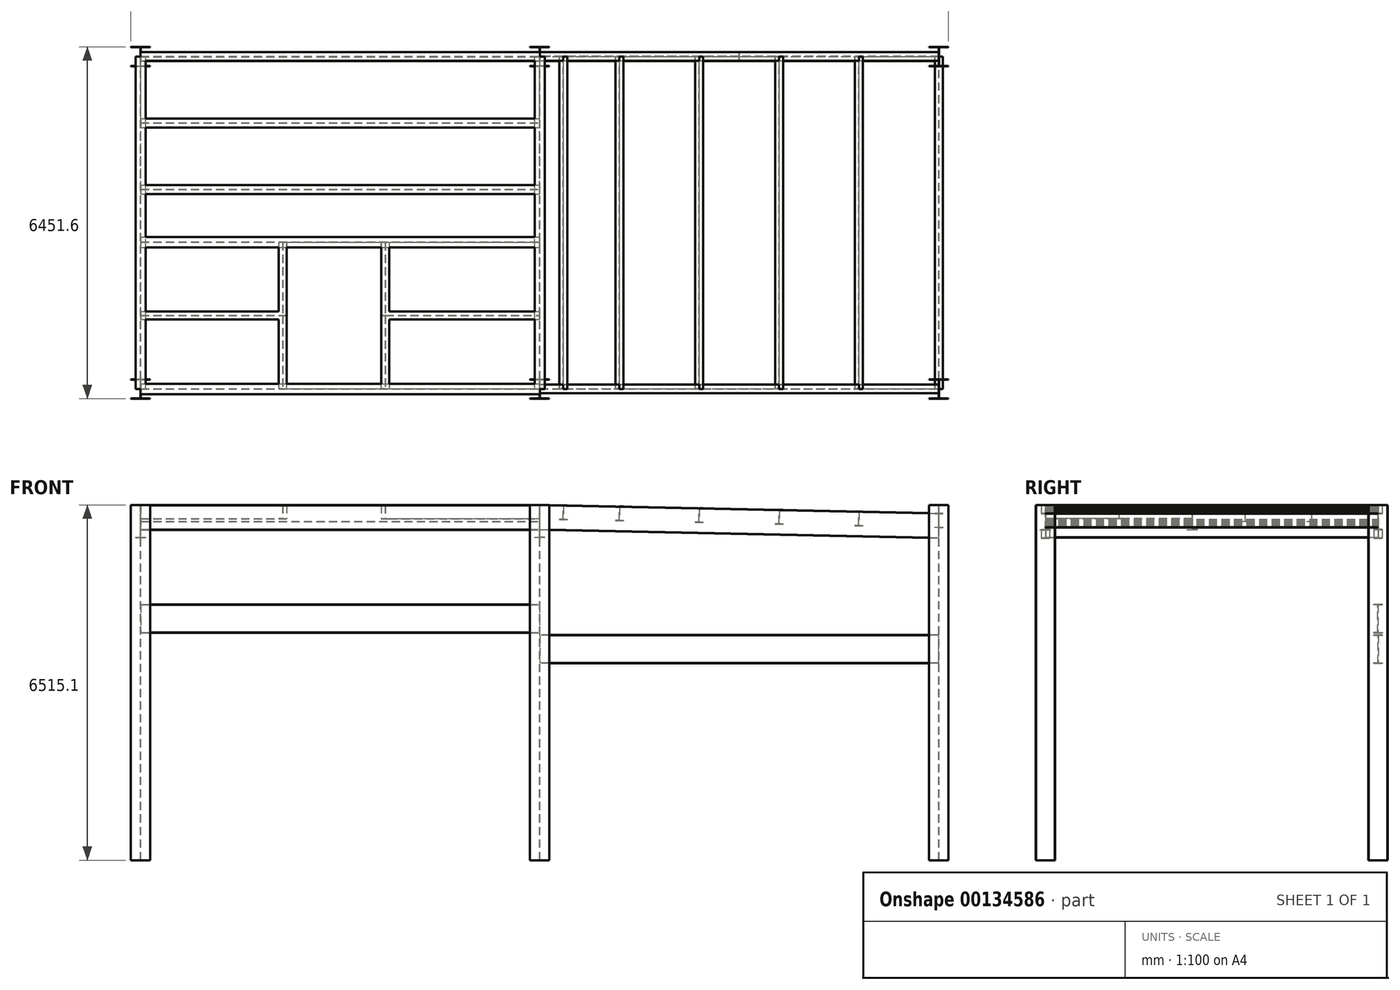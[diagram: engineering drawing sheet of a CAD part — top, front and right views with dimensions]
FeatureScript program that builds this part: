
annotation { "Feature Type Name" : "Feature", "Feature Type Description" : "" }
export const myFeature = defineFeature(function(context is Context, id is Id, definition is map)
    precondition{}
    {
        {
            var Q0;
            Q0=qCreatedBy(makeId("Top.planeOp"),FACE);
            var sketch = newSketch(context, id + "F0", { "sketchPlane" : qUnion([Q0])});
            skLineSegment(sketch, "E0", {"start": v(0, 0) * mm, "end": v(0, 177.8) * mm, "construction": true});
            skLineSegment(sketch, "E1", {"start": v(0, 0) * mm, "end": v(-3.18, 0) * mm, "construction": true});
            skLineSegment(sketch, "E2", {"start": v(0, 177.8) * mm, "end": v(-177.8, 177.8) * mm});
            skLineSegment(sketch, "E3", {"start": v(-177.8, 177.8) * mm, "end": v(-177.8, 171.45) * mm});
            skLineSegment(sketch, "E4", {"start": v(-177.8, 171.45) * mm, "end": v(-3.17, 171.45) * mm});
            skLineSegment(sketch, "E5", {"start": v(-3.17, 171.45) * mm, "end": v(-3.17, 0) * mm});
            skLineSegment(sketch, "E6.MirrorCS", {"start": v(177.8, 177.8) * mm, "end": v(177.8, 171.45) * mm});
            skLineSegment(sketch, "E7.MirrorCS", {"start": v(0, 177.8) * mm, "end": v(177.8, 177.8) * mm});
            skLineSegment(sketch, "E8.MirrorCS", {"start": v(3.17, 171.45) * mm, "end": v(3.17, 0) * mm});
            skLineSegment(sketch, "E9.MirrorCS", {"start": v(177.8, 171.45) * mm, "end": v(3.17, 171.45) * mm});
            skLineSegment(sketch, "E10.MirrorCS", {"start": v(-177.8, -171.45) * mm, "end": v(-3.18, -171.45) * mm});
            skLineSegment(sketch, "E11.MirrorCS", {"start": v(-3.17, -171.45) * mm, "end": v(-3.17, 0) * mm});
            skLineSegment(sketch, "E12.MirrorCS", {"start": v(0, -177.8) * mm, "end": v(177.8, -177.8) * mm});
            skLineSegment(sketch, "E13.MirrorCS", {"start": v(3.18, -171.45) * mm, "end": v(3.17, 0) * mm});
            skLineSegment(sketch, "E14.MirrorCS", {"start": v(177.8, -177.8) * mm, "end": v(177.8, -171.45) * mm});
            skLineSegment(sketch, "E15.MirrorCS", {"start": v(177.8, -171.45) * mm, "end": v(3.18, -171.45) * mm});
            skLineSegment(sketch, "E16.MirrorCS", {"start": v(-177.8, -177.8) * mm, "end": v(-177.8, -171.45) * mm});
            skLineSegment(sketch, "E17.MirrorCS", {"start": v(0, -177.8) * mm, "end": v(-177.8, -177.8) * mm});
            skLineSegment(sketch, "E18", {"start": v(-3.17, 171.45) * mm, "end": v(3.17, 171.45) * mm, "construction": true});
            skLineSegment(sketch, "E19.0.1.0", {"start": v(0, -6096) * mm, "end": v(0, -5918.2) * mm, "construction": true});
            skLineSegment(sketch, "E19.0.1.1", {"start": v(177.8, -5924.55) * mm, "end": v(3.17, -5924.55) * mm});
            skLineSegment(sketch, "E19.0.1.2", {"start": v(-3.17, -5924.55) * mm, "end": v(-3.17, -6096) * mm});
            skLineSegment(sketch, "E19.0.1.3", {"start": v(-177.8, -5924.55) * mm, "end": v(-3.17, -5924.55) * mm});
            skLineSegment(sketch, "E19.0.1.4", {"start": v(0, -5918.2) * mm, "end": v(177.8, -5918.2) * mm});
            skLineSegment(sketch, "E19.0.1.5", {"start": v(0, -6273.8) * mm, "end": v(-177.8, -6273.8) * mm});
            skLineSegment(sketch, "E19.0.1.6", {"start": v(3.17, -5924.55) * mm, "end": v(3.17, -6096) * mm});
            skLineSegment(sketch, "E19.0.1.7", {"start": v(-177.8, -6267.45) * mm, "end": v(-3.18, -6267.45) * mm});
            skLineSegment(sketch, "E19.0.1.8", {"start": v(3.18, -6267.45) * mm, "end": v(3.17, -6096) * mm});
            skLineSegment(sketch, "E19.0.1.9", {"start": v(-3.17, -6267.45) * mm, "end": v(-3.17, -6096) * mm});
            skLineSegment(sketch, "E19.0.1.10", {"start": v(0, -6273.8) * mm, "end": v(177.8, -6273.8) * mm});
            skLineSegment(sketch, "E19.0.1.11", {"start": v(0, -5918.2) * mm, "end": v(-177.8, -5918.2) * mm});
            skLineSegment(sketch, "E19.0.1.12", {"start": v(177.8, -6267.45) * mm, "end": v(3.18, -6267.45) * mm});
            skLineSegment(sketch, "E19.0.1.13", {"start": v(177.8, -6273.8) * mm, "end": v(177.8, -6267.45) * mm});
            skLineSegment(sketch, "E19.0.1.14", {"start": v(177.8, -5918.2) * mm, "end": v(177.8, -5924.55) * mm});
            skLineSegment(sketch, "E19.0.1.15", {"start": v(-177.8, -5918.2) * mm, "end": v(-177.8, -5924.55) * mm});
            skLineSegment(sketch, "E19.0.1.16", {"start": v(-177.8, -6273.8) * mm, "end": v(-177.8, -6267.45) * mm});
            skLineSegment(sketch, "E19.0.1.17", {"start": v(0, -6096) * mm, "end": v(-3.17, -6096) * mm, "construction": true});
            skLineSegment(sketch, "E19.0.1.18", {"start": v(-3.17, -5924.55) * mm, "end": v(3.17, -5924.55) * mm, "construction": true});
            skLineSegment(sketch, "E19.1.0.0", {"start": v(-7315.2, 0) * mm, "end": v(-7315.2, 177.8) * mm, "construction": true});
            skLineSegment(sketch, "E19.1.0.1", {"start": v(-7137.4, 171.45) * mm, "end": v(-7312.03, 171.45) * mm});
            skLineSegment(sketch, "E19.1.0.2", {"start": v(-7318.38, 171.45) * mm, "end": v(-7318.38, 0) * mm});
            skLineSegment(sketch, "E19.1.0.3", {"start": v(-7493, 171.45) * mm, "end": v(-7318.38, 171.45) * mm});
            skLineSegment(sketch, "E19.1.0.4", {"start": v(-7315.2, 177.8) * mm, "end": v(-7137.4, 177.8) * mm});
            skLineSegment(sketch, "E19.1.0.5", {"start": v(-7315.2, -177.8) * mm, "end": v(-7493, -177.8) * mm});
            skLineSegment(sketch, "E19.1.0.6", {"start": v(-7312.03, 171.45) * mm, "end": v(-7312.03, 0) * mm});
            skLineSegment(sketch, "E19.1.0.7", {"start": v(-7493, -171.45) * mm, "end": v(-7318.38, -171.45) * mm});
            skLineSegment(sketch, "E19.1.0.8", {"start": v(-7312.03, -171.45) * mm, "end": v(-7312.03, 0) * mm});
            skLineSegment(sketch, "E19.1.0.9", {"start": v(-7318.38, -171.45) * mm, "end": v(-7318.38, 0) * mm});
            skLineSegment(sketch, "E19.1.0.10", {"start": v(-7315.2, -177.8) * mm, "end": v(-7137.4, -177.8) * mm});
            skLineSegment(sketch, "E19.1.0.11", {"start": v(-7315.2, 177.8) * mm, "end": v(-7493, 177.8) * mm});
            skLineSegment(sketch, "E19.1.0.12", {"start": v(-7137.4, -171.45) * mm, "end": v(-7312.03, -171.45) * mm});
            skLineSegment(sketch, "E19.1.0.13", {"start": v(-7137.4, -177.8) * mm, "end": v(-7137.4, -171.45) * mm});
            skLineSegment(sketch, "E19.1.0.14", {"start": v(-7137.4, 177.8) * mm, "end": v(-7137.4, 171.45) * mm});
            skLineSegment(sketch, "E19.1.0.15", {"start": v(-7493, 177.8) * mm, "end": v(-7493, 171.45) * mm});
            skLineSegment(sketch, "E19.1.0.16", {"start": v(-7493, -177.8) * mm, "end": v(-7493, -171.45) * mm});
            skLineSegment(sketch, "E19.1.0.17", {"start": v(-7315.2, 0) * mm, "end": v(-7318.38, 0) * mm, "construction": true});
            skLineSegment(sketch, "E19.1.0.18", {"start": v(-7318.38, 171.45) * mm, "end": v(-7312.03, 171.45) * mm, "construction": true});
            skLineSegment(sketch, "E19.1.1.0", {"start": v(-7315.2, -6096) * mm, "end": v(-7315.2, -5918.2) * mm, "construction": true});
            skLineSegment(sketch, "E19.1.1.1", {"start": v(-7137.4, -5924.55) * mm, "end": v(-7312.03, -5924.55) * mm});
            skLineSegment(sketch, "E19.1.1.2", {"start": v(-7318.38, -5924.55) * mm, "end": v(-7318.38, -6096) * mm});
            skLineSegment(sketch, "E19.1.1.3", {"start": v(-7493, -5924.55) * mm, "end": v(-7318.38, -5924.55) * mm});
            skLineSegment(sketch, "E19.1.1.4", {"start": v(-7315.2, -5918.2) * mm, "end": v(-7137.4, -5918.2) * mm});
            skLineSegment(sketch, "E19.1.1.5", {"start": v(-7315.2, -6273.8) * mm, "end": v(-7493, -6273.8) * mm});
            skLineSegment(sketch, "E19.1.1.6", {"start": v(-7312.03, -5924.55) * mm, "end": v(-7312.03, -6096) * mm});
            skLineSegment(sketch, "E19.1.1.7", {"start": v(-7493, -6267.45) * mm, "end": v(-7318.38, -6267.45) * mm});
            skLineSegment(sketch, "E19.1.1.8", {"start": v(-7312.03, -6267.45) * mm, "end": v(-7312.03, -6096) * mm});
            skLineSegment(sketch, "E19.1.1.9", {"start": v(-7318.38, -6267.45) * mm, "end": v(-7318.38, -6096) * mm});
            skLineSegment(sketch, "E19.1.1.10", {"start": v(-7315.2, -6273.8) * mm, "end": v(-7137.4, -6273.8) * mm});
            skLineSegment(sketch, "E19.1.1.11", {"start": v(-7315.2, -5918.2) * mm, "end": v(-7493, -5918.2) * mm});
            skLineSegment(sketch, "E19.1.1.12", {"start": v(-7137.4, -6267.45) * mm, "end": v(-7312.03, -6267.45) * mm});
            skLineSegment(sketch, "E19.1.1.13", {"start": v(-7137.4, -6273.8) * mm, "end": v(-7137.4, -6267.45) * mm});
            skLineSegment(sketch, "E19.1.1.14", {"start": v(-7137.4, -5918.2) * mm, "end": v(-7137.4, -5924.55) * mm});
            skLineSegment(sketch, "E19.1.1.15", {"start": v(-7493, -5918.2) * mm, "end": v(-7493, -5924.55) * mm});
            skLineSegment(sketch, "E19.1.1.16", {"start": v(-7493, -6273.8) * mm, "end": v(-7493, -6267.45) * mm});
            skLineSegment(sketch, "E19.1.1.17", {"start": v(-7315.2, -6096) * mm, "end": v(-7318.38, -6096) * mm, "construction": true});
            skLineSegment(sketch, "E19.1.1.18", {"start": v(-7318.38, -5924.55) * mm, "end": v(-7312.03, -5924.55) * mm, "construction": true});
            skLineSegment(sketch, "E19.direction1", {"start": v(-177.8, -177.8) * mm, "end": v(-7493, -177.8) * mm, "construction": true});
            skLineSegment(sketch, "E19.direction2", {"start": v(-177.8, -177.8) * mm, "end": v(-177.8, -6273.8) * mm, "construction": true});
            skLineSegment(sketch, "E20.1.0.0", {"start": v(7315.2, -5918.2) * mm, "end": v(7493, -5918.2) * mm});
            skLineSegment(sketch, "E20.1.0.1", {"start": v(7315.2, -6273.8) * mm, "end": v(7137.4, -6273.8) * mm});
            skLineSegment(sketch, "E20.1.0.2", {"start": v(7312.03, -5924.55) * mm, "end": v(7312.03, -6096) * mm});
            skLineSegment(sketch, "E20.1.0.3", {"start": v(7137.4, -5924.55) * mm, "end": v(7312.03, -5924.55) * mm});
            skLineSegment(sketch, "E20.1.0.4", {"start": v(7315.2, -6096) * mm, "end": v(7315.2, -5918.2) * mm, "construction": true});
            skLineSegment(sketch, "E20.1.0.5", {"start": v(7315.2, -6273.8) * mm, "end": v(7493, -6273.8) * mm});
            skLineSegment(sketch, "E20.1.0.6", {"start": v(7315.2, -5918.2) * mm, "end": v(7137.4, -5918.2) * mm});
            skLineSegment(sketch, "E20.1.0.7", {"start": v(7318.38, -6267.45) * mm, "end": v(7318.38, -6096) * mm});
            skLineSegment(sketch, "E20.1.0.8", {"start": v(7312.03, -6267.45) * mm, "end": v(7312.03, -6096) * mm});
            skLineSegment(sketch, "E20.1.0.9", {"start": v(7493, -6267.45) * mm, "end": v(7318.38, -6267.45) * mm});
            skLineSegment(sketch, "E20.1.0.10", {"start": v(7493, -5924.55) * mm, "end": v(7318.38, -5924.55) * mm});
            skLineSegment(sketch, "E20.1.0.11", {"start": v(7137.4, -6267.45) * mm, "end": v(7312.03, -6267.45) * mm});
            skLineSegment(sketch, "E20.1.0.12", {"start": v(7318.38, -5924.55) * mm, "end": v(7318.38, -6096) * mm});
            skLineSegment(sketch, "E20.1.0.13", {"start": v(7493, -6273.8) * mm, "end": v(7493, -6267.45) * mm});
            skLineSegment(sketch, "E20.1.0.14", {"start": v(7493, -5918.2) * mm, "end": v(7493, -5924.55) * mm});
            skLineSegment(sketch, "E20.1.0.15", {"start": v(7137.4, -5918.2) * mm, "end": v(7137.4, -5924.55) * mm});
            skLineSegment(sketch, "E20.1.0.16", {"start": v(7312.03, -5924.55) * mm, "end": v(7318.38, -5924.55) * mm, "construction": true});
            skLineSegment(sketch, "E20.1.0.17", {"start": v(7137.4, -6273.8) * mm, "end": v(7137.4, -6267.45) * mm});
            skLineSegment(sketch, "E20.1.0.18", {"start": v(7315.2, -6096) * mm, "end": v(7312.03, -6096) * mm, "construction": true});
            skLineSegment(sketch, "E20.1.0.19", {"start": v(7315.2, -177.8) * mm, "end": v(7137.4, -177.8) * mm});
            skLineSegment(sketch, "E20.1.0.20", {"start": v(7493, -171.45) * mm, "end": v(7318.38, -171.45) * mm});
            skLineSegment(sketch, "E20.1.0.21", {"start": v(7315.2, 0) * mm, "end": v(7315.2, 177.8) * mm, "construction": true});
            skLineSegment(sketch, "E20.1.0.22", {"start": v(7137.4, 171.45) * mm, "end": v(7312.03, 171.45) * mm});
            skLineSegment(sketch, "E20.1.0.23", {"start": v(7493, 171.45) * mm, "end": v(7318.38, 171.45) * mm});
            skLineSegment(sketch, "E20.1.0.24", {"start": v(7137.4, -171.45) * mm, "end": v(7312.03, -171.45) * mm});
            skLineSegment(sketch, "E20.1.0.25", {"start": v(7312.03, -171.45) * mm, "end": v(7312.03, 0) * mm});
            skLineSegment(sketch, "E20.1.0.26", {"start": v(7315.2, -177.8) * mm, "end": v(7493, -177.8) * mm});
            skLineSegment(sketch, "E20.1.0.27", {"start": v(7318.38, -171.45) * mm, "end": v(7318.38, 0) * mm});
            skLineSegment(sketch, "E20.1.0.28", {"start": v(7315.2, 177.8) * mm, "end": v(7137.4, 177.8) * mm});
            skLineSegment(sketch, "E20.1.0.29", {"start": v(7315.2, 177.8) * mm, "end": v(7493, 177.8) * mm});
            skLineSegment(sketch, "E20.1.0.30", {"start": v(7318.38, 171.45) * mm, "end": v(7318.38, 0) * mm});
            skLineSegment(sketch, "E20.1.0.31", {"start": v(7493, -177.8) * mm, "end": v(7493, -171.45) * mm});
            skLineSegment(sketch, "E20.1.0.32", {"start": v(7312.03, 171.45) * mm, "end": v(7312.03, 0) * mm});
            skLineSegment(sketch, "E20.1.0.33", {"start": v(7137.4, -177.8) * mm, "end": v(7137.4, -171.45) * mm});
            skLineSegment(sketch, "E20.1.0.34", {"start": v(7137.4, 177.8) * mm, "end": v(7137.4, 171.45) * mm});
            skLineSegment(sketch, "E20.1.0.35", {"start": v(7493, 177.8) * mm, "end": v(7493, 171.45) * mm});
            skLineSegment(sketch, "E20.1.0.36", {"start": v(7315.2, 0) * mm, "end": v(7312.03, 0) * mm, "construction": true});
            skLineSegment(sketch, "E20.1.0.37", {"start": v(7312.03, 171.45) * mm, "end": v(7318.38, 171.45) * mm, "construction": true});
            skLineSegment(sketch, "E20.direction1", {"start": v(-177.8, -6273.8) * mm, "end": v(7137.4, -6273.8) * mm, "construction": true});
            skSolve(sketch);
        }
        {
            var Q0;
            Q0 = qSketchRegion(id + "F0", true);
            extrude(context, id + "F1", {"entities" : qUnion([Q0]), "oppositeDirection" : true, "depth" : 6515.1 * mm});
        }
        {
            var Q0;
            Q0=qCreatedBy(makeId("Right.planeOp"),FACE);
            var sketch = newSketch(context, id + "F2", { "sketchPlane" : qUnion([Q0])});
            skLineSegment(sketch, "E21", {"start": v(0, -227.33) * mm, "end": v(0, 0) * mm, "construction": true});
            skLineSegment(sketch, "E22", {"start": v(0, -227.33) * mm, "end": v(-3.18, -227.33) * mm, "construction": true});
            skLineSegment(sketch, "E23", {"start": v(0, 0) * mm, "end": v(-76.4, 0) * mm});
            skLineSegment(sketch, "E24", {"start": v(-76.4, 0) * mm, "end": v(-76.4, -6.35) * mm});
            skLineSegment(sketch, "E25", {"start": v(-76.4, -6.35) * mm, "end": v(-3.18, -6.35) * mm});
            skLineSegment(sketch, "E26", {"start": v(-3.18, -6.35) * mm, "end": v(-3.18, -227.33) * mm});
            skLineSegment(sketch, "E27.MirrorCS", {"start": v(76.4, 0) * mm, "end": v(76.4, -6.35) * mm});
            skLineSegment(sketch, "E28.MirrorCS", {"start": v(0, 0) * mm, "end": v(76.4, 0) * mm});
            skLineSegment(sketch, "E29.MirrorCS", {"start": v(3.18, -6.35) * mm, "end": v(3.18, -227.33) * mm});
            skLineSegment(sketch, "E30.MirrorCS", {"start": v(76.4, -6.35) * mm, "end": v(3.17, -6.35) * mm});
            skLineSegment(sketch, "E31.MirrorCS", {"start": v(-76.4, -448.3) * mm, "end": v(-3.17, -448.3) * mm});
            skLineSegment(sketch, "E32.MirrorCS", {"start": v(-3.18, -448.3) * mm, "end": v(-3.18, -227.33) * mm});
            skLineSegment(sketch, "E33.MirrorCS", {"start": v(0, -454.66) * mm, "end": v(76.4, -454.66) * mm});
            skLineSegment(sketch, "E34.MirrorCS", {"start": v(3.18, -448.3) * mm, "end": v(3.18, -227.33) * mm});
            skLineSegment(sketch, "E35.MirrorCS", {"start": v(76.4, -454.66) * mm, "end": v(76.4, -448.3) * mm});
            skLineSegment(sketch, "E36.MirrorCS", {"start": v(76.4, -448.3) * mm, "end": v(3.17, -448.3) * mm});
            skLineSegment(sketch, "E37.MirrorCS", {"start": v(-76.4, -454.66) * mm, "end": v(-76.4, -448.3) * mm});
            skLineSegment(sketch, "E38.MirrorCS", {"start": v(0, -454.66) * mm, "end": v(-76.4, -454.66) * mm});
            skLineSegment(sketch, "E39", {"start": v(-3.18, -6.35) * mm, "end": v(3.17, -6.35) * mm, "construction": true});
            skLineSegment(sketch, "E40.0.0", {"start": v(171.45, 0) * mm, "end": v(-171.45, 0) * mm, "construction": true});
            skLineSegment(sketch, "E40.0.1", {"start": v(-171.45, 0) * mm, "end": v(-171.45, -6515.1) * mm, "construction": true});
            skLineSegment(sketch, "E40.0.2", {"start": v(-171.45, -6515.1) * mm, "end": v(171.45, -6515.1) * mm, "construction": true});
            skLineSegment(sketch, "E40.0.3", {"start": v(171.45, -6515.1) * mm, "end": v(171.45, 0) * mm, "construction": true});
            skPoint(sketch, "E41", {"position": v(0, 0) * mm});
            skLineSegment(sketch, "E42", {"start": v(0, 0) * mm, "end": v(-1219.2, 0) * mm, "construction": true});
            skLineSegment(sketch, "E43", {"start": v(-1219.2, 0) * mm, "end": v(-2438.4, 0) * mm, "construction": true});
            skLineSegment(sketch, "E44", {"start": v(-2438.4, 0) * mm, "end": v(-3403.6, 0) * mm, "construction": true});
            skLineSegment(sketch, "E45", {"start": v(-3403.6, 0) * mm, "end": v(-4749.8, 0) * mm, "construction": true});
            skLineSegment(sketch, "E46", {"start": v(-4749.8, 0) * mm, "end": v(-6096, 0) * mm, "construction": true});
            skLineSegment(sketch, "E47.0", {"start": v(-6267.45, 0) * mm, "end": v(-5924.55, 0) * mm, "construction": true});
            skPoint(sketch, "E48", {"position": v(-6096, 0) * mm});
            skLineSegment(sketch, "E49", {"start": v(-1219.2, -155.2) * mm, "end": v(-1219.2, 0) * mm, "construction": true});
            skLineSegment(sketch, "E50", {"start": v(-1219.2, -155.2) * mm, "end": v(-1222.38, -155.2) * mm, "construction": true});
            skLineSegment(sketch, "E51", {"start": v(-1219.2, 0) * mm, "end": v(-1301.62, 0) * mm});
            skLineSegment(sketch, "E52", {"start": v(-1301.62, 0) * mm, "end": v(-1301.62, -6.35) * mm});
            skLineSegment(sketch, "E53", {"start": v(-1301.62, -6.35) * mm, "end": v(-1222.38, -6.35) * mm});
            skLineSegment(sketch, "E54", {"start": v(-1222.38, -6.35) * mm, "end": v(-1222.38, -155.2) * mm});
            skLineSegment(sketch, "E55.MirrorCS", {"start": v(-1136.78, 0) * mm, "end": v(-1136.78, -6.35) * mm});
            skLineSegment(sketch, "E56.MirrorCS", {"start": v(-1219.2, 0) * mm, "end": v(-1136.78, 0) * mm});
            skLineSegment(sketch, "E57.MirrorCS", {"start": v(-1216.03, -6.35) * mm, "end": v(-1216.03, -155.2) * mm});
            skLineSegment(sketch, "E58.MirrorCS", {"start": v(-1136.78, -6.35) * mm, "end": v(-1216.02, -6.35) * mm});
            skLineSegment(sketch, "E59.MirrorCS", {"start": v(-1301.62, -304.04) * mm, "end": v(-1222.38, -304.04) * mm});
            skLineSegment(sketch, "E60.MirrorCS", {"start": v(-1222.38, -304.04) * mm, "end": v(-1222.38, -155.2) * mm});
            skLineSegment(sketch, "E61.MirrorCS", {"start": v(-1219.2, -310.39) * mm, "end": v(-1136.78, -310.39) * mm});
            skLineSegment(sketch, "E62.MirrorCS", {"start": v(-1216.03, -304.04) * mm, "end": v(-1216.03, -155.2) * mm});
            skLineSegment(sketch, "E63.MirrorCS", {"start": v(-1136.78, -310.39) * mm, "end": v(-1136.78, -304.04) * mm});
            skLineSegment(sketch, "E64.MirrorCS", {"start": v(-1136.78, -304.04) * mm, "end": v(-1216.02, -304.04) * mm});
            skLineSegment(sketch, "E65.MirrorCS", {"start": v(-1301.62, -310.39) * mm, "end": v(-1301.62, -304.04) * mm});
            skLineSegment(sketch, "E66.MirrorCS", {"start": v(-1219.2, -310.39) * mm, "end": v(-1301.62, -310.39) * mm});
            skLineSegment(sketch, "E67", {"start": v(-1222.38, -6.35) * mm, "end": v(-1216.02, -6.35) * mm, "construction": true});
            skPoint(sketch, "E68", {"position": v(-1219.2, 0) * mm});
            skLineSegment(sketch, "E69", {"start": v(-2438.4, -155.2) * mm, "end": v(-2438.4, 0) * mm, "construction": true});
            skLineSegment(sketch, "E70", {"start": v(-2438.4, -155.2) * mm, "end": v(-2441.57, -155.2) * mm, "construction": true});
            skLineSegment(sketch, "E71", {"start": v(-2438.4, 0) * mm, "end": v(-2520.82, 0) * mm});
            skLineSegment(sketch, "E72", {"start": v(-2520.82, 0) * mm, "end": v(-2520.82, -6.35) * mm});
            skLineSegment(sketch, "E73", {"start": v(-2520.82, -6.35) * mm, "end": v(-2441.57, -6.35) * mm});
            skLineSegment(sketch, "E74", {"start": v(-2441.57, -6.35) * mm, "end": v(-2441.57, -155.2) * mm});
            skLineSegment(sketch, "E75.MirrorCS", {"start": v(-2355.98, 0) * mm, "end": v(-2355.98, -6.35) * mm});
            skLineSegment(sketch, "E76.MirrorCS", {"start": v(-2438.4, 0) * mm, "end": v(-2355.98, 0) * mm});
            skLineSegment(sketch, "E77.MirrorCS", {"start": v(-2435.23, -6.35) * mm, "end": v(-2435.23, -155.2) * mm});
            skLineSegment(sketch, "E78.MirrorCS", {"start": v(-2355.98, -6.35) * mm, "end": v(-2435.22, -6.35) * mm});
            skLineSegment(sketch, "E79.MirrorCS", {"start": v(-2520.82, -304.04) * mm, "end": v(-2441.58, -304.04) * mm});
            skLineSegment(sketch, "E80.MirrorCS", {"start": v(-2441.57, -304.04) * mm, "end": v(-2441.57, -155.2) * mm});
            skLineSegment(sketch, "E81.MirrorCS", {"start": v(-2438.4, -310.39) * mm, "end": v(-2355.98, -310.39) * mm});
            skLineSegment(sketch, "E82.MirrorCS", {"start": v(-2435.23, -304.04) * mm, "end": v(-2435.23, -155.2) * mm});
            skLineSegment(sketch, "E83.MirrorCS", {"start": v(-2355.98, -310.39) * mm, "end": v(-2355.98, -304.04) * mm});
            skLineSegment(sketch, "E84.MirrorCS", {"start": v(-2355.98, -304.04) * mm, "end": v(-2435.22, -304.04) * mm});
            skLineSegment(sketch, "E85.MirrorCS", {"start": v(-2520.82, -310.39) * mm, "end": v(-2520.82, -304.04) * mm});
            skLineSegment(sketch, "E86.MirrorCS", {"start": v(-2438.4, -310.39) * mm, "end": v(-2520.82, -310.39) * mm});
            skLineSegment(sketch, "E87", {"start": v(-2441.57, -6.35) * mm, "end": v(-2435.22, -6.35) * mm, "construction": true});
            skPoint(sketch, "E88", {"position": v(-2438.4, 0) * mm});
            skLineSegment(sketch, "E89", {"start": v(-3403.6, -228.47) * mm, "end": v(-3403.6, 0) * mm, "construction": true});
            skLineSegment(sketch, "E90", {"start": v(-3403.6, -228.47) * mm, "end": v(-3406.78, -228.47) * mm, "construction": true});
            skLineSegment(sketch, "E91", {"start": v(-3403.6, 0) * mm, "end": v(-3498.79, 0) * mm});
            skLineSegment(sketch, "E92", {"start": v(-3498.79, 0) * mm, "end": v(-3498.79, -6.35) * mm});
            skLineSegment(sketch, "E93", {"start": v(-3498.79, -6.35) * mm, "end": v(-3406.78, -6.35) * mm});
            skLineSegment(sketch, "E94", {"start": v(-3406.78, -6.35) * mm, "end": v(-3406.78, -228.47) * mm});
            skLineSegment(sketch, "E95.MirrorCS", {"start": v(-3308.41, 0) * mm, "end": v(-3308.41, -6.35) * mm});
            skLineSegment(sketch, "E96.MirrorCS", {"start": v(-3403.6, 0) * mm, "end": v(-3308.41, 0) * mm});
            skLineSegment(sketch, "E97.MirrorCS", {"start": v(-3400.43, -6.35) * mm, "end": v(-3400.43, -228.47) * mm});
            skLineSegment(sketch, "E98.MirrorCS", {"start": v(-3308.41, -6.35) * mm, "end": v(-3400.43, -6.35) * mm});
            skLineSegment(sketch, "E99.MirrorCS", {"start": v(-3498.79, -450.6) * mm, "end": v(-3406.77, -450.6) * mm});
            skLineSegment(sketch, "E100.MirrorCS", {"start": v(-3406.78, -450.6) * mm, "end": v(-3406.78, -228.47) * mm});
            skLineSegment(sketch, "E101.MirrorCS", {"start": v(-3403.6, -456.95) * mm, "end": v(-3308.41, -456.95) * mm});
            skLineSegment(sketch, "E102.MirrorCS", {"start": v(-3400.43, -450.6) * mm, "end": v(-3400.43, -228.47) * mm});
            skLineSegment(sketch, "E103.MirrorCS", {"start": v(-3308.41, -456.95) * mm, "end": v(-3308.41, -450.6) * mm});
            skLineSegment(sketch, "E104.MirrorCS", {"start": v(-3308.41, -450.6) * mm, "end": v(-3400.43, -450.6) * mm});
            skLineSegment(sketch, "E105.MirrorCS", {"start": v(-3498.79, -456.95) * mm, "end": v(-3498.79, -450.6) * mm});
            skLineSegment(sketch, "E106.MirrorCS", {"start": v(-3403.6, -456.95) * mm, "end": v(-3498.79, -456.95) * mm});
            skLineSegment(sketch, "E107", {"start": v(-3406.78, -6.35) * mm, "end": v(-3400.43, -6.35) * mm, "construction": true});
            skPoint(sketch, "E108", {"position": v(-3403.6, 0) * mm});
            skLineSegment(sketch, "E109", {"start": v(-4749.8, -129.16) * mm, "end": v(-4749.8, 0) * mm, "construction": true});
            skLineSegment(sketch, "E110", {"start": v(-4749.8, -129.16) * mm, "end": v(-4752.98, -129.16) * mm, "construction": true});
            skLineSegment(sketch, "E111", {"start": v(-4749.8, 0) * mm, "end": v(-4822.82, 0) * mm});
            skLineSegment(sketch, "E112", {"start": v(-4822.82, 0) * mm, "end": v(-4822.82, -6.35) * mm});
            skLineSegment(sketch, "E113", {"start": v(-4822.82, -6.35) * mm, "end": v(-4752.98, -6.35) * mm});
            skLineSegment(sketch, "E114", {"start": v(-4752.98, -6.35) * mm, "end": v(-4752.98, -129.16) * mm});
            skLineSegment(sketch, "E115.MirrorCS", {"start": v(-4676.78, 0) * mm, "end": v(-4676.78, -6.35) * mm});
            skLineSegment(sketch, "E116.MirrorCS", {"start": v(-4749.8, 0) * mm, "end": v(-4676.78, 0) * mm});
            skLineSegment(sketch, "E117.MirrorCS", {"start": v(-4746.63, -6.35) * mm, "end": v(-4746.63, -129.16) * mm});
            skLineSegment(sketch, "E118.MirrorCS", {"start": v(-4676.78, -6.35) * mm, "end": v(-4746.62, -6.35) * mm});
            skLineSegment(sketch, "E119.MirrorCS", {"start": v(-4822.82, -251.97) * mm, "end": v(-4752.98, -251.97) * mm});
            skLineSegment(sketch, "E120.MirrorCS", {"start": v(-4752.98, -251.97) * mm, "end": v(-4752.98, -129.16) * mm});
            skLineSegment(sketch, "E121.MirrorCS", {"start": v(-4749.8, -258.32) * mm, "end": v(-4676.78, -258.32) * mm});
            skLineSegment(sketch, "E122.MirrorCS", {"start": v(-4746.63, -251.97) * mm, "end": v(-4746.63, -129.16) * mm});
            skLineSegment(sketch, "E123.MirrorCS", {"start": v(-4676.78, -258.32) * mm, "end": v(-4676.78, -251.97) * mm});
            skLineSegment(sketch, "E124.MirrorCS", {"start": v(-4676.78, -251.97) * mm, "end": v(-4746.62, -251.97) * mm});
            skLineSegment(sketch, "E125.MirrorCS", {"start": v(-4822.82, -258.32) * mm, "end": v(-4822.82, -251.97) * mm});
            skLineSegment(sketch, "E126.MirrorCS", {"start": v(-4749.8, -258.32) * mm, "end": v(-4822.82, -258.32) * mm});
            skLineSegment(sketch, "E127", {"start": v(-4752.98, -6.35) * mm, "end": v(-4746.62, -6.35) * mm, "construction": true});
            skPoint(sketch, "E128", {"position": v(-4749.8, 0) * mm});
            skLineSegment(sketch, "E129", {"start": v(-6096, -228.47) * mm, "end": v(-6096, 0) * mm, "construction": true});
            skLineSegment(sketch, "E130", {"start": v(-6096, -228.47) * mm, "end": v(-6099.18, -228.47) * mm, "construction": true});
            skLineSegment(sketch, "E131", {"start": v(-6096, 0) * mm, "end": v(-6191.19, 0) * mm});
            skLineSegment(sketch, "E132", {"start": v(-6191.19, 0) * mm, "end": v(-6191.19, -6.35) * mm});
            skLineSegment(sketch, "E133", {"start": v(-6191.19, -6.35) * mm, "end": v(-6099.18, -6.35) * mm});
            skLineSegment(sketch, "E134", {"start": v(-6099.18, -6.35) * mm, "end": v(-6099.18, -228.47) * mm});
            skLineSegment(sketch, "E135.MirrorCS", {"start": v(-6000.81, 0) * mm, "end": v(-6000.81, -6.35) * mm});
            skLineSegment(sketch, "E136.MirrorCS", {"start": v(-6096, 0) * mm, "end": v(-6000.81, 0) * mm});
            skLineSegment(sketch, "E137.MirrorCS", {"start": v(-6092.83, -6.35) * mm, "end": v(-6092.83, -228.47) * mm});
            skLineSegment(sketch, "E138.MirrorCS", {"start": v(-6000.81, -6.35) * mm, "end": v(-6092.83, -6.35) * mm});
            skLineSegment(sketch, "E139.MirrorCS", {"start": v(-6191.19, -450.6) * mm, "end": v(-6099.18, -450.6) * mm});
            skLineSegment(sketch, "E140.MirrorCS", {"start": v(-6099.18, -450.6) * mm, "end": v(-6099.18, -228.47) * mm});
            skLineSegment(sketch, "E141.MirrorCS", {"start": v(-6096, -456.95) * mm, "end": v(-6000.81, -456.95) * mm});
            skLineSegment(sketch, "E142.MirrorCS", {"start": v(-6092.83, -450.6) * mm, "end": v(-6092.83, -228.47) * mm});
            skLineSegment(sketch, "E143.MirrorCS", {"start": v(-6000.81, -456.95) * mm, "end": v(-6000.81, -450.6) * mm});
            skLineSegment(sketch, "E144.MirrorCS", {"start": v(-6000.81, -450.6) * mm, "end": v(-6092.83, -450.6) * mm});
            skLineSegment(sketch, "E145.MirrorCS", {"start": v(-6191.19, -456.95) * mm, "end": v(-6191.19, -450.6) * mm});
            skLineSegment(sketch, "E146.MirrorCS", {"start": v(-6096, -456.95) * mm, "end": v(-6191.19, -456.95) * mm});
            skLineSegment(sketch, "E147", {"start": v(-6099.18, -6.35) * mm, "end": v(-6092.83, -6.35) * mm, "construction": true});
            skLineSegment(sketch, "E148", {"start": v(-3.17, -2084.83) * mm, "end": v(-3.17, -1822.45) * mm, "construction": true});
            skLineSegment(sketch, "E149", {"start": v(-3.17, -2084.83) * mm, "end": v(-6.35, -2084.83) * mm, "construction": true});
            skLineSegment(sketch, "E150", {"start": v(-3.17, -1822.45) * mm, "end": v(-85.72, -1822.45) * mm});
            skLineSegment(sketch, "E151", {"start": v(-85.72, -1822.45) * mm, "end": v(-85.72, -1828.8) * mm});
            skLineSegment(sketch, "E152", {"start": v(-85.72, -1828.8) * mm, "end": v(-6.35, -1828.8) * mm});
            skLineSegment(sketch, "E153", {"start": v(-6.35, -1828.8) * mm, "end": v(-6.35, -2084.83) * mm});
            skLineSegment(sketch, "E154.MirrorCS", {"start": v(79.38, -1822.45) * mm, "end": v(79.38, -1828.8) * mm});
            skLineSegment(sketch, "E155.MirrorCS", {"start": v(-3.17, -1822.45) * mm, "end": v(79.38, -1822.45) * mm});
            skLineSegment(sketch, "E156.MirrorCS", {"start": v(0, -1828.8) * mm, "end": v(0, -2084.83) * mm});
            skLineSegment(sketch, "E157.MirrorCS", {"start": v(79.38, -1828.8) * mm, "end": v(0, -1828.8) * mm});
            skLineSegment(sketch, "E158.MirrorCS", {"start": v(-85.72, -2340.86) * mm, "end": v(-6.35, -2340.86) * mm});
            skLineSegment(sketch, "E159.MirrorCS", {"start": v(-6.35, -2340.86) * mm, "end": v(-6.35, -2084.83) * mm});
            skLineSegment(sketch, "E160.MirrorCS", {"start": v(-3.17, -2347.21) * mm, "end": v(79.38, -2347.21) * mm});
            skLineSegment(sketch, "E161.MirrorCS", {"start": v(0, -2340.86) * mm, "end": v(0, -2084.83) * mm});
            skLineSegment(sketch, "E162.MirrorCS", {"start": v(79.38, -2347.21) * mm, "end": v(79.38, -2340.86) * mm});
            skLineSegment(sketch, "E163.MirrorCS", {"start": v(79.37, -2340.86) * mm, "end": v(0, -2340.86) * mm});
            skLineSegment(sketch, "E164.MirrorCS", {"start": v(-85.72, -2347.21) * mm, "end": v(-85.72, -2340.86) * mm});
            skLineSegment(sketch, "E165.MirrorCS", {"start": v(-3.17, -2347.21) * mm, "end": v(-85.73, -2347.21) * mm});
            skLineSegment(sketch, "E166", {"start": v(-6.35, -1828.8) * mm, "end": v(0, -1828.8) * mm, "construction": true});
            skPoint(sketch, "E167", {"position": v(-3.17, -1822.45) * mm});
            skLineSegment(sketch, "E168", {"start": v(0, 0) * mm, "end": v(-3.17, -1822.45) * mm, "construction": true});
            skSolve(sketch);
        }
        {
            var Q0;
            Q0 = qSketchRegion(id + "F2", true);
            extrude(context, id + "F3", {"entities" : qUnion([Q0]), "oppositeDirection" : true, "depth" : 7315.2 * mm});
        }
        {
            var Q0;
            Q0=qCreatedBy(makeId("Right.planeOp"),FACE);
            var sketch = newSketch(context, id + "F4", { "sketchPlane" : qUnion([Q0])});
            skLineSegment(sketch, "E169.0", {"start": v(-171.45, 0) * mm, "end": v(171.45, 0) * mm, "construction": true});
            skPoint(sketch, "E170", {"position": v(0, 0) * mm});
            skLineSegment(sketch, "E171", {"start": v(0, 0) * mm, "end": v(0, -2381.25) * mm, "construction": true});
            skLineSegment(sketch, "E172", {"start": v(0, -2643.63) * mm, "end": v(0, -2381.25) * mm, "construction": true});
            skLineSegment(sketch, "E173", {"start": v(0, -2643.63) * mm, "end": v(-3.17, -2643.63) * mm, "construction": true});
            skLineSegment(sketch, "E174", {"start": v(0, -2381.25) * mm, "end": v(-82.55, -2381.25) * mm});
            skLineSegment(sketch, "E175", {"start": v(-82.55, -2381.25) * mm, "end": v(-82.55, -2387.6) * mm});
            skLineSegment(sketch, "E176", {"start": v(-82.55, -2387.6) * mm, "end": v(-3.17, -2387.6) * mm});
            skLineSegment(sketch, "E177", {"start": v(-3.17, -2387.6) * mm, "end": v(-3.17, -2643.63) * mm});
            skLineSegment(sketch, "E178.MirrorCS", {"start": v(82.55, -2381.25) * mm, "end": v(82.55, -2387.6) * mm});
            skLineSegment(sketch, "E179.MirrorCS", {"start": v(0, -2381.25) * mm, "end": v(82.55, -2381.25) * mm});
            skLineSegment(sketch, "E180.MirrorCS", {"start": v(3.18, -2387.6) * mm, "end": v(3.18, -2643.63) * mm});
            skLineSegment(sketch, "E181.MirrorCS", {"start": v(82.55, -2387.6) * mm, "end": v(3.17, -2387.6) * mm});
            skLineSegment(sketch, "E182.MirrorCS", {"start": v(-82.55, -2899.66) * mm, "end": v(-3.17, -2899.66) * mm});
            skLineSegment(sketch, "E183.MirrorCS", {"start": v(-3.17, -2899.66) * mm, "end": v(-3.17, -2643.63) * mm});
            skLineSegment(sketch, "E184.MirrorCS", {"start": v(0, -2906.01) * mm, "end": v(82.55, -2906.01) * mm});
            skLineSegment(sketch, "E185.MirrorCS", {"start": v(3.18, -2899.66) * mm, "end": v(3.18, -2643.63) * mm});
            skLineSegment(sketch, "E186.MirrorCS", {"start": v(82.55, -2906.01) * mm, "end": v(82.55, -2899.66) * mm});
            skLineSegment(sketch, "E187.MirrorCS", {"start": v(82.55, -2899.66) * mm, "end": v(3.17, -2899.66) * mm});
            skLineSegment(sketch, "E188.MirrorCS", {"start": v(-82.55, -2906.01) * mm, "end": v(-82.55, -2899.66) * mm});
            skLineSegment(sketch, "E189.MirrorCS", {"start": v(0, -2906.01) * mm, "end": v(-82.55, -2906.01) * mm});
            skLineSegment(sketch, "E190", {"start": v(-3.17, -2387.6) * mm, "end": v(3.17, -2387.6) * mm, "construction": true});
            skPoint(sketch, "E191", {"position": v(0, -2381.25) * mm});
            skSolve(sketch);
        }
        {
            var Q0;
            Q0 = qSketchRegion(id + "F4", true);
            extrude(context, id + "F5", {"entities" : qUnion([Q0]), "depth" : 7315.2 * mm});
        }
        {
            var Q0;
            Q0=qCreatedBy(makeId("Front.planeOp"),FACE);
            var sketch = newSketch(context, id + "F6", { "sketchPlane" : qUnion([Q0])});
            skLineSegment(sketch, "E192.0", {"start": v(-177.8, 0) * mm, "end": v(177.8, 0) * mm, "construction": true});
            skLineSegment(sketch, "E193.0", {"start": v(-7493, 0) * mm, "end": v(-7137.4, 0) * mm, "construction": true});
            skPoint(sketch, "E194", {"position": v(-7315.2, 0) * mm});
            skPoint(sketch, "E195", {"position": v(0, 0) * mm});
            skLineSegment(sketch, "E196.0", {"start": v(7137.4, 0) * mm, "end": v(7493, 0) * mm, "construction": true});
            skPoint(sketch, "E197", {"position": v(7315.2, 0) * mm});
            skLineSegment(sketch, "E198", {"start": v(7315.2, 0) * mm, "end": v(7315.2, -154.5) * mm, "construction": true});
            skLineSegment(sketch, "E199", {"start": v(0, 0) * mm, "end": v(431.7, -9.12) * mm, "construction": true});
            skLineSegment(sketch, "E200", {"start": v(431.7, -9.12) * mm, "end": v(1460.38, -30.85) * mm, "construction": true});
            skLineSegment(sketch, "E201", {"start": v(1460.38, -30.85) * mm, "end": v(2924.09, -61.76) * mm, "construction": true});
            skLineSegment(sketch, "E202", {"start": v(2924.09, -61.76) * mm, "end": v(4387.8, -92.68) * mm, "construction": true});
            skLineSegment(sketch, "E203", {"start": v(4387.8, -92.68) * mm, "end": v(5851.5, -123.6) * mm, "construction": true});
            skLineSegment(sketch, "E204", {"start": v(5851.5, -123.6) * mm, "end": v(7315.2, -154.5) * mm, "construction": true});
            skLineSegment(sketch, "E205", {"start": v(431.7, -138.28) * mm, "end": v(431.7, -9.12) * mm, "construction": true});
            skLineSegment(sketch, "E206", {"start": v(431.7, -138.28) * mm, "end": v(428.53, -138.28) * mm, "construction": true});
            skLineSegment(sketch, "E207", {"start": v(431.7, -9.12) * mm, "end": v(358.68, -9.12) * mm});
            skLineSegment(sketch, "E208", {"start": v(358.68, -9.12) * mm, "end": v(358.68, -15.47) * mm});
            skLineSegment(sketch, "E209", {"start": v(358.68, -15.47) * mm, "end": v(428.53, -15.47) * mm});
            skLineSegment(sketch, "E210", {"start": v(428.53, -15.47) * mm, "end": v(428.53, -138.28) * mm});
            skLineSegment(sketch, "E211.MirrorCS", {"start": v(504.73, -9.12) * mm, "end": v(504.73, -15.47) * mm});
            skLineSegment(sketch, "E212.MirrorCS", {"start": v(431.7, -9.12) * mm, "end": v(504.73, -9.12) * mm});
            skLineSegment(sketch, "E213.MirrorCS", {"start": v(434.88, -15.47) * mm, "end": v(434.88, -138.28) * mm});
            skLineSegment(sketch, "E214.MirrorCS", {"start": v(504.73, -15.47) * mm, "end": v(434.88, -15.47) * mm});
            skLineSegment(sketch, "E215.MirrorCS", {"start": v(358.68, -261.09) * mm, "end": v(428.53, -261.09) * mm});
            skLineSegment(sketch, "E216.MirrorCS", {"start": v(428.53, -261.09) * mm, "end": v(428.53, -138.28) * mm});
            skLineSegment(sketch, "E217.MirrorCS", {"start": v(431.7, -267.44) * mm, "end": v(504.73, -267.44) * mm});
            skLineSegment(sketch, "E218.MirrorCS", {"start": v(434.88, -261.09) * mm, "end": v(434.88, -138.28) * mm});
            skLineSegment(sketch, "E219.MirrorCS", {"start": v(504.73, -267.44) * mm, "end": v(504.73, -261.09) * mm});
            skLineSegment(sketch, "E220.MirrorCS", {"start": v(504.73, -261.09) * mm, "end": v(434.88, -261.09) * mm});
            skLineSegment(sketch, "E221.MirrorCS", {"start": v(358.68, -267.44) * mm, "end": v(358.68, -261.09) * mm});
            skLineSegment(sketch, "E222.MirrorCS", {"start": v(431.7, -267.44) * mm, "end": v(358.68, -267.44) * mm});
            skLineSegment(sketch, "E223", {"start": v(428.53, -15.47) * mm, "end": v(434.88, -15.47) * mm, "construction": true});
            skPoint(sketch, "E224", {"position": v(431.7, -9.12) * mm});
            skLineSegment(sketch, "E225", {"start": v(1460.38, -160) * mm, "end": v(1460.38, -30.85) * mm, "construction": true});
            skLineSegment(sketch, "E226", {"start": v(1460.38, -160) * mm, "end": v(1457.2, -160) * mm, "construction": true});
            skLineSegment(sketch, "E227", {"start": v(1460.38, -30.85) * mm, "end": v(1387.36, -30.85) * mm});
            skLineSegment(sketch, "E228", {"start": v(1387.36, -30.85) * mm, "end": v(1387.36, -37.2) * mm});
            skLineSegment(sketch, "E229", {"start": v(1387.36, -37.2) * mm, "end": v(1457.2, -37.2) * mm});
            skLineSegment(sketch, "E230", {"start": v(1457.2, -37.2) * mm, "end": v(1457.2, -160) * mm});
            skLineSegment(sketch, "E231.MirrorCS", {"start": v(1533.4, -30.85) * mm, "end": v(1533.4, -37.2) * mm});
            skLineSegment(sketch, "E232.MirrorCS", {"start": v(1460.38, -30.85) * mm, "end": v(1533.4, -30.85) * mm});
            skLineSegment(sketch, "E233.MirrorCS", {"start": v(1463.56, -37.2) * mm, "end": v(1463.56, -160) * mm});
            skLineSegment(sketch, "E234.MirrorCS", {"start": v(1533.4, -37.2) * mm, "end": v(1463.56, -37.2) * mm});
            skLineSegment(sketch, "E235.MirrorCS", {"start": v(1387.36, -282.81) * mm, "end": v(1457.2, -282.81) * mm});
            skLineSegment(sketch, "E236.MirrorCS", {"start": v(1457.2, -282.81) * mm, "end": v(1457.2, -160) * mm});
            skLineSegment(sketch, "E237.MirrorCS", {"start": v(1460.38, -289.16) * mm, "end": v(1533.4, -289.16) * mm});
            skLineSegment(sketch, "E238.MirrorCS", {"start": v(1463.56, -282.81) * mm, "end": v(1463.56, -160) * mm});
            skLineSegment(sketch, "E239.MirrorCS", {"start": v(1533.4, -289.16) * mm, "end": v(1533.4, -282.81) * mm});
            skLineSegment(sketch, "E240.MirrorCS", {"start": v(1533.4, -282.81) * mm, "end": v(1463.56, -282.81) * mm});
            skLineSegment(sketch, "E241.MirrorCS", {"start": v(1387.36, -289.16) * mm, "end": v(1387.36, -282.81) * mm});
            skLineSegment(sketch, "E242.MirrorCS", {"start": v(1460.38, -289.16) * mm, "end": v(1387.36, -289.16) * mm});
            skLineSegment(sketch, "E243", {"start": v(1457.2, -37.2) * mm, "end": v(1463.56, -37.2) * mm, "construction": true});
            skPoint(sketch, "E244", {"position": v(1460.38, -30.85) * mm});
            skLineSegment(sketch, "E245", {"start": v(2924.09, -190.92) * mm, "end": v(2924.09, -61.76) * mm, "construction": true});
            skLineSegment(sketch, "E246", {"start": v(2924.09, -190.92) * mm, "end": v(2920.91, -190.92) * mm, "construction": true});
            skLineSegment(sketch, "E247", {"start": v(2924.09, -61.76) * mm, "end": v(2851.06, -61.76) * mm});
            skLineSegment(sketch, "E248", {"start": v(2851.06, -61.76) * mm, "end": v(2851.06, -68.11) * mm});
            skLineSegment(sketch, "E249", {"start": v(2851.06, -68.11) * mm, "end": v(2920.91, -68.11) * mm});
            skLineSegment(sketch, "E250", {"start": v(2920.91, -68.11) * mm, "end": v(2920.91, -190.92) * mm});
            skLineSegment(sketch, "E251.MirrorCS", {"start": v(2997.11, -61.76) * mm, "end": v(2997.11, -68.11) * mm});
            skLineSegment(sketch, "E252.MirrorCS", {"start": v(2924.09, -61.76) * mm, "end": v(2997.11, -61.76) * mm});
            skLineSegment(sketch, "E253.MirrorCS", {"start": v(2927.26, -68.11) * mm, "end": v(2927.26, -190.92) * mm});
            skLineSegment(sketch, "E254.MirrorCS", {"start": v(2997.11, -68.11) * mm, "end": v(2927.26, -68.11) * mm});
            skLineSegment(sketch, "E255.MirrorCS", {"start": v(2851.06, -313.73) * mm, "end": v(2920.91, -313.73) * mm});
            skLineSegment(sketch, "E256.MirrorCS", {"start": v(2920.91, -313.73) * mm, "end": v(2920.91, -190.92) * mm});
            skLineSegment(sketch, "E257.MirrorCS", {"start": v(2924.09, -320.08) * mm, "end": v(2997.11, -320.08) * mm});
            skLineSegment(sketch, "E258.MirrorCS", {"start": v(2927.26, -313.73) * mm, "end": v(2927.26, -190.92) * mm});
            skLineSegment(sketch, "E259.MirrorCS", {"start": v(2997.11, -320.08) * mm, "end": v(2997.11, -313.73) * mm});
            skLineSegment(sketch, "E260.MirrorCS", {"start": v(2997.11, -313.73) * mm, "end": v(2927.26, -313.73) * mm});
            skLineSegment(sketch, "E261.MirrorCS", {"start": v(2851.06, -320.08) * mm, "end": v(2851.06, -313.73) * mm});
            skLineSegment(sketch, "E262.MirrorCS", {"start": v(2924.09, -320.08) * mm, "end": v(2851.06, -320.08) * mm});
            skLineSegment(sketch, "E263", {"start": v(2920.91, -68.11) * mm, "end": v(2927.26, -68.11) * mm, "construction": true});
            skPoint(sketch, "E264", {"position": v(2924.09, -61.76) * mm});
            skLineSegment(sketch, "E265", {"start": v(4387.8, -221.84) * mm, "end": v(4387.8, -92.68) * mm, "construction": true});
            skLineSegment(sketch, "E266", {"start": v(4387.8, -221.84) * mm, "end": v(4384.62, -221.84) * mm, "construction": true});
            skLineSegment(sketch, "E267", {"start": v(4387.8, -92.68) * mm, "end": v(4314.77, -92.68) * mm});
            skLineSegment(sketch, "E268", {"start": v(4314.77, -92.68) * mm, "end": v(4314.77, -99.03) * mm});
            skLineSegment(sketch, "E269", {"start": v(4314.77, -99.03) * mm, "end": v(4384.62, -99.03) * mm});
            skLineSegment(sketch, "E270", {"start": v(4384.62, -99.03) * mm, "end": v(4384.62, -221.84) * mm});
            skLineSegment(sketch, "E271.MirrorCS", {"start": v(4460.82, -92.68) * mm, "end": v(4460.82, -99.03) * mm});
            skLineSegment(sketch, "E272.MirrorCS", {"start": v(4387.8, -92.68) * mm, "end": v(4460.82, -92.68) * mm});
            skLineSegment(sketch, "E273.MirrorCS", {"start": v(4390.97, -99.03) * mm, "end": v(4390.97, -221.84) * mm});
            skLineSegment(sketch, "E274.MirrorCS", {"start": v(4460.82, -99.03) * mm, "end": v(4390.97, -99.03) * mm});
            skLineSegment(sketch, "E275.MirrorCS", {"start": v(4314.77, -344.64) * mm, "end": v(4384.62, -344.64) * mm});
            skLineSegment(sketch, "E276.MirrorCS", {"start": v(4384.62, -344.64) * mm, "end": v(4384.62, -221.84) * mm});
            skLineSegment(sketch, "E277.MirrorCS", {"start": v(4387.8, -351) * mm, "end": v(4460.82, -351) * mm});
            skLineSegment(sketch, "E278.MirrorCS", {"start": v(4390.97, -344.64) * mm, "end": v(4390.97, -221.84) * mm});
            skLineSegment(sketch, "E279.MirrorCS", {"start": v(4460.82, -351) * mm, "end": v(4460.82, -344.64) * mm});
            skLineSegment(sketch, "E280.MirrorCS", {"start": v(4460.82, -344.64) * mm, "end": v(4390.97, -344.64) * mm});
            skLineSegment(sketch, "E281.MirrorCS", {"start": v(4314.77, -351) * mm, "end": v(4314.77, -344.64) * mm});
            skLineSegment(sketch, "E282.MirrorCS", {"start": v(4387.8, -351) * mm, "end": v(4314.77, -351) * mm});
            skLineSegment(sketch, "E283", {"start": v(4384.62, -99.03) * mm, "end": v(4390.97, -99.03) * mm, "construction": true});
            skPoint(sketch, "E284", {"position": v(4387.8, -92.68) * mm});
            skLineSegment(sketch, "E285", {"start": v(5851.5, -252.75) * mm, "end": v(5851.5, -123.6) * mm, "construction": true});
            skLineSegment(sketch, "E286", {"start": v(5851.5, -252.75) * mm, "end": v(5848.32, -252.75) * mm, "construction": true});
            skLineSegment(sketch, "E287", {"start": v(5851.5, -123.6) * mm, "end": v(5778.47, -123.6) * mm});
            skLineSegment(sketch, "E288", {"start": v(5778.47, -123.6) * mm, "end": v(5778.47, -129.94) * mm});
            skLineSegment(sketch, "E289", {"start": v(5778.47, -129.94) * mm, "end": v(5848.32, -129.94) * mm});
            skLineSegment(sketch, "E290", {"start": v(5848.32, -129.94) * mm, "end": v(5848.32, -252.75) * mm});
            skLineSegment(sketch, "E291.MirrorCS", {"start": v(5924.52, -123.6) * mm, "end": v(5924.52, -129.94) * mm});
            skLineSegment(sketch, "E292.MirrorCS", {"start": v(5851.5, -123.6) * mm, "end": v(5924.52, -123.6) * mm});
            skLineSegment(sketch, "E293.MirrorCS", {"start": v(5854.67, -129.94) * mm, "end": v(5854.67, -252.75) * mm});
            skLineSegment(sketch, "E294.MirrorCS", {"start": v(5924.52, -129.94) * mm, "end": v(5854.67, -129.94) * mm});
            skLineSegment(sketch, "E295.MirrorCS", {"start": v(5778.47, -375.56) * mm, "end": v(5848.32, -375.56) * mm});
            skLineSegment(sketch, "E296.MirrorCS", {"start": v(5848.32, -375.56) * mm, "end": v(5848.32, -252.75) * mm});
            skLineSegment(sketch, "E297.MirrorCS", {"start": v(5851.5, -381.91) * mm, "end": v(5924.52, -381.91) * mm});
            skLineSegment(sketch, "E298.MirrorCS", {"start": v(5854.67, -375.56) * mm, "end": v(5854.67, -252.75) * mm});
            skLineSegment(sketch, "E299.MirrorCS", {"start": v(5924.52, -381.91) * mm, "end": v(5924.52, -375.56) * mm});
            skLineSegment(sketch, "E300.MirrorCS", {"start": v(5924.52, -375.56) * mm, "end": v(5854.67, -375.56) * mm});
            skLineSegment(sketch, "E301.MirrorCS", {"start": v(5778.47, -381.91) * mm, "end": v(5778.47, -375.56) * mm});
            skLineSegment(sketch, "E302.MirrorCS", {"start": v(5851.5, -381.91) * mm, "end": v(5778.47, -381.91) * mm});
            skLineSegment(sketch, "E303", {"start": v(5848.32, -129.94) * mm, "end": v(5854.67, -129.94) * mm, "construction": true});
            skPoint(sketch, "E304", {"position": v(5851.5, -123.6) * mm});
            skLineSegment(sketch, "E305", {"start": v(1463.56, -37.2) * mm, "end": v(0, 0) * mm, "construction": true});
            skLineSegment(sketch, "E306", {"start": v(7315.2, -283.67) * mm, "end": v(7315.2, -154.5) * mm, "construction": true});
            skLineSegment(sketch, "E307", {"start": v(7315.2, -283.67) * mm, "end": v(7312.03, -283.67) * mm, "construction": true});
            skLineSegment(sketch, "E308", {"start": v(7315.2, -154.5) * mm, "end": v(7242.18, -154.5) * mm});
            skLineSegment(sketch, "E309", {"start": v(7242.18, -154.5) * mm, "end": v(7242.18, -160.86) * mm});
            skLineSegment(sketch, "E310", {"start": v(7242.18, -160.86) * mm, "end": v(7312.03, -160.86) * mm});
            skLineSegment(sketch, "E311", {"start": v(7312.03, -160.86) * mm, "end": v(7312.03, -283.67) * mm});
            skLineSegment(sketch, "E312.MirrorCS", {"start": v(7388.23, -154.5) * mm, "end": v(7388.23, -160.86) * mm});
            skLineSegment(sketch, "E313.MirrorCS", {"start": v(7315.2, -154.5) * mm, "end": v(7388.23, -154.5) * mm});
            skLineSegment(sketch, "E314.MirrorCS", {"start": v(7318.38, -160.86) * mm, "end": v(7318.38, -283.67) * mm});
            skLineSegment(sketch, "E315.MirrorCS", {"start": v(7388.23, -160.86) * mm, "end": v(7318.38, -160.86) * mm});
            skLineSegment(sketch, "E316.MirrorCS", {"start": v(7242.18, -406.48) * mm, "end": v(7312.03, -406.48) * mm});
            skLineSegment(sketch, "E317.MirrorCS", {"start": v(7312.03, -406.48) * mm, "end": v(7312.03, -283.67) * mm});
            skLineSegment(sketch, "E318.MirrorCS", {"start": v(7315.2, -412.83) * mm, "end": v(7388.23, -412.83) * mm});
            skLineSegment(sketch, "E319.MirrorCS", {"start": v(7318.38, -406.48) * mm, "end": v(7318.38, -283.67) * mm});
            skLineSegment(sketch, "E320.MirrorCS", {"start": v(7388.23, -412.83) * mm, "end": v(7388.23, -406.48) * mm});
            skLineSegment(sketch, "E321.MirrorCS", {"start": v(7388.23, -406.48) * mm, "end": v(7318.38, -406.48) * mm});
            skLineSegment(sketch, "E322.MirrorCS", {"start": v(7242.18, -412.83) * mm, "end": v(7242.18, -406.48) * mm});
            skLineSegment(sketch, "E323.MirrorCS", {"start": v(7315.2, -412.83) * mm, "end": v(7242.18, -412.83) * mm});
            skLineSegment(sketch, "E324", {"start": v(7312.03, -160.86) * mm, "end": v(7318.38, -160.86) * mm, "construction": true});
            skPoint(sketch, "E325", {"position": v(7315.2, -154.5) * mm});
            skLineSegment(sketch, "E326", {"start": v(0, -299.34) * mm, "end": v(0, 0) * mm, "construction": true});
            skLineSegment(sketch, "E327", {"start": v(0, -299.34) * mm, "end": v(-3.17, -299.34) * mm, "construction": true});
            skLineSegment(sketch, "E328", {"start": v(0, 0) * mm, "end": v(-88.96, 0) * mm});
            skLineSegment(sketch, "E329", {"start": v(-88.96, 0) * mm, "end": v(-88.96, -6.35) * mm});
            skLineSegment(sketch, "E330", {"start": v(-88.96, -6.35) * mm, "end": v(-3.18, -6.35) * mm});
            skLineSegment(sketch, "E331", {"start": v(-3.18, -6.35) * mm, "end": v(-3.18, -299.34) * mm});
            skLineSegment(sketch, "E332.MirrorCS", {"start": v(88.96, 0) * mm, "end": v(88.96, -6.35) * mm});
            skLineSegment(sketch, "E333.MirrorCS", {"start": v(0, 0) * mm, "end": v(88.96, 0) * mm});
            skLineSegment(sketch, "E334.MirrorCS", {"start": v(3.17, -6.35) * mm, "end": v(3.17, -299.34) * mm});
            skLineSegment(sketch, "E335.MirrorCS", {"start": v(88.96, -6.35) * mm, "end": v(3.17, -6.35) * mm});
            skLineSegment(sketch, "E336.MirrorCS", {"start": v(-88.96, -592.33) * mm, "end": v(-3.17, -592.33) * mm});
            skLineSegment(sketch, "E337.MirrorCS", {"start": v(-3.17, -592.33) * mm, "end": v(-3.18, -299.34) * mm});
            skLineSegment(sketch, "E338.MirrorCS", {"start": v(0, -598.68) * mm, "end": v(88.96, -598.68) * mm});
            skLineSegment(sketch, "E339.MirrorCS", {"start": v(3.17, -592.33) * mm, "end": v(3.17, -299.34) * mm});
            skLineSegment(sketch, "E340.MirrorCS", {"start": v(88.96, -598.68) * mm, "end": v(88.96, -592.33) * mm});
            skLineSegment(sketch, "E341.MirrorCS", {"start": v(88.96, -592.33) * mm, "end": v(3.17, -592.33) * mm});
            skLineSegment(sketch, "E342.MirrorCS", {"start": v(-88.96, -598.68) * mm, "end": v(-88.96, -592.33) * mm});
            skLineSegment(sketch, "E343.MirrorCS", {"start": v(0, -598.68) * mm, "end": v(-88.96, -598.68) * mm});
            skLineSegment(sketch, "E344", {"start": v(-3.18, -6.35) * mm, "end": v(3.17, -6.35) * mm, "construction": true});
            skLineSegment(sketch, "E345", {"start": v(-7315.2, -299.34) * mm, "end": v(-7315.2, 0) * mm, "construction": true});
            skLineSegment(sketch, "E346", {"start": v(-7315.2, -299.34) * mm, "end": v(-7318.38, -299.34) * mm, "construction": true});
            skLineSegment(sketch, "E347", {"start": v(-7315.2, 0) * mm, "end": v(-7404.16, 0) * mm});
            skLineSegment(sketch, "E348", {"start": v(-7404.16, 0) * mm, "end": v(-7404.16, -6.35) * mm});
            skLineSegment(sketch, "E349", {"start": v(-7404.16, -6.35) * mm, "end": v(-7318.38, -6.35) * mm});
            skLineSegment(sketch, "E350", {"start": v(-7318.38, -6.35) * mm, "end": v(-7318.38, -299.34) * mm});
            skLineSegment(sketch, "E351.MirrorCS", {"start": v(-7226.24, 0) * mm, "end": v(-7226.24, -6.35) * mm});
            skLineSegment(sketch, "E352.MirrorCS", {"start": v(-7315.2, 0) * mm, "end": v(-7226.24, 0) * mm});
            skLineSegment(sketch, "E353.MirrorCS", {"start": v(-7312.03, -6.35) * mm, "end": v(-7312.03, -299.34) * mm});
            skLineSegment(sketch, "E354.MirrorCS", {"start": v(-7226.24, -6.35) * mm, "end": v(-7312.03, -6.35) * mm});
            skLineSegment(sketch, "E355.MirrorCS", {"start": v(-7404.16, -592.33) * mm, "end": v(-7318.38, -592.33) * mm});
            skLineSegment(sketch, "E356.MirrorCS", {"start": v(-7318.38, -592.33) * mm, "end": v(-7318.38, -299.34) * mm});
            skLineSegment(sketch, "E357.MirrorCS", {"start": v(-7315.2, -598.68) * mm, "end": v(-7226.24, -598.68) * mm});
            skLineSegment(sketch, "E358.MirrorCS", {"start": v(-7312.03, -592.33) * mm, "end": v(-7312.03, -299.34) * mm});
            skLineSegment(sketch, "E359.MirrorCS", {"start": v(-7226.24, -598.68) * mm, "end": v(-7226.24, -592.33) * mm});
            skLineSegment(sketch, "E360.MirrorCS", {"start": v(-7226.24, -592.33) * mm, "end": v(-7312.03, -592.33) * mm});
            skLineSegment(sketch, "E361.MirrorCS", {"start": v(-7404.16, -598.68) * mm, "end": v(-7404.16, -592.33) * mm});
            skLineSegment(sketch, "E362.MirrorCS", {"start": v(-7315.2, -598.68) * mm, "end": v(-7404.16, -598.68) * mm});
            skLineSegment(sketch, "E363", {"start": v(-7318.38, -6.35) * mm, "end": v(-7312.03, -6.35) * mm, "construction": true});
            skSolve(sketch);
        }
        {
            var Q0;
            Q0 = qSketchRegion(id + "F6", true);
            extrude(context, id + "F7", {"entities" : qUnion([Q0]), "depth" : 6096 * mm});
        }
        {
            var Q0;
            Q0=qCreatedBy(makeId("Right.planeOp"),FACE);
            var sketch = newSketch(context, id + "F8", { "sketchPlane" : qUnion([Q0])});
            skLineSegment(sketch, "E364.0", {"start": v(-171.45, 0) * mm, "end": v(171.45, 0) * mm, "construction": true});
            skLineSegment(sketch, "E365.0", {"start": v(-6267.45, 0) * mm, "end": v(-5924.55, 0) * mm, "construction": true});
            skPoint(sketch, "E366", {"position": v(-6096, 0) * mm});
            skPoint(sketch, "E367", {"position": v(0, 0) * mm});
            skLineSegment(sketch, "E368", {"start": v(0, -227.33) * mm, "end": v(0, 0) * mm, "construction": true});
            skLineSegment(sketch, "E369", {"start": v(0, -227.33) * mm, "end": v(-3.18, -227.33) * mm, "construction": true});
            skLineSegment(sketch, "E370", {"start": v(0, 0) * mm, "end": v(-76.4, 0) * mm});
            skLineSegment(sketch, "E371", {"start": v(-76.4, 0) * mm, "end": v(-76.4, -6.35) * mm});
            skLineSegment(sketch, "E372", {"start": v(-76.4, -6.35) * mm, "end": v(-3.17, -6.35) * mm});
            skLineSegment(sketch, "E373", {"start": v(-3.17, -6.35) * mm, "end": v(-3.17, -227.33) * mm});
            skLineSegment(sketch, "E374.MirrorCS", {"start": v(76.4, 0) * mm, "end": v(76.4, -6.35) * mm});
            skLineSegment(sketch, "E375.MirrorCS", {"start": v(0, 0) * mm, "end": v(76.4, 0) * mm});
            skLineSegment(sketch, "E376.MirrorCS", {"start": v(3.17, -6.35) * mm, "end": v(3.18, -227.33) * mm});
            skLineSegment(sketch, "E377.MirrorCS", {"start": v(76.4, -6.35) * mm, "end": v(3.17, -6.35) * mm});
            skLineSegment(sketch, "E378.MirrorCS", {"start": v(-76.4, -448.3) * mm, "end": v(-3.18, -448.3) * mm});
            skLineSegment(sketch, "E379.MirrorCS", {"start": v(-3.17, -448.3) * mm, "end": v(-3.17, -227.33) * mm});
            skLineSegment(sketch, "E380.MirrorCS", {"start": v(0, -454.66) * mm, "end": v(76.4, -454.66) * mm});
            skLineSegment(sketch, "E381.MirrorCS", {"start": v(3.18, -448.3) * mm, "end": v(3.17, -227.33) * mm});
            skLineSegment(sketch, "E382.MirrorCS", {"start": v(76.4, -454.66) * mm, "end": v(76.4, -448.3) * mm});
            skLineSegment(sketch, "E383.MirrorCS", {"start": v(76.4, -448.3) * mm, "end": v(3.18, -448.3) * mm});
            skLineSegment(sketch, "E384.MirrorCS", {"start": v(-76.4, -454.66) * mm, "end": v(-76.4, -448.3) * mm});
            skLineSegment(sketch, "E385.MirrorCS", {"start": v(0, -454.66) * mm, "end": v(-76.4, -454.66) * mm});
            skLineSegment(sketch, "E386", {"start": v(-3.17, -6.35) * mm, "end": v(3.17, -6.35) * mm, "construction": true});
            skLineSegment(sketch, "E387", {"start": v(-6096, -227.33) * mm, "end": v(-6096, 0) * mm, "construction": true});
            skLineSegment(sketch, "E388", {"start": v(-6096, -227.33) * mm, "end": v(-6099.18, -227.33) * mm, "construction": true});
            skLineSegment(sketch, "E389", {"start": v(-6096, 0) * mm, "end": v(-6172.4, 0) * mm});
            skLineSegment(sketch, "E390", {"start": v(-6172.4, 0) * mm, "end": v(-6172.4, -6.35) * mm});
            skLineSegment(sketch, "E391", {"start": v(-6172.4, -6.35) * mm, "end": v(-6099.18, -6.35) * mm});
            skLineSegment(sketch, "E392", {"start": v(-6099.18, -6.35) * mm, "end": v(-6099.18, -227.33) * mm});
            skLineSegment(sketch, "E393.MirrorCS", {"start": v(-6019.6, 0) * mm, "end": v(-6019.6, -6.35) * mm});
            skLineSegment(sketch, "E394.MirrorCS", {"start": v(-6096, 0) * mm, "end": v(-6019.6, 0) * mm});
            skLineSegment(sketch, "E395.MirrorCS", {"start": v(-6092.83, -6.35) * mm, "end": v(-6092.83, -227.33) * mm});
            skLineSegment(sketch, "E396.MirrorCS", {"start": v(-6019.6, -6.35) * mm, "end": v(-6092.83, -6.35) * mm});
            skLineSegment(sketch, "E397.MirrorCS", {"start": v(-6172.4, -448.3) * mm, "end": v(-6099.18, -448.3) * mm});
            skLineSegment(sketch, "E398.MirrorCS", {"start": v(-6099.18, -448.3) * mm, "end": v(-6099.18, -227.33) * mm});
            skLineSegment(sketch, "E399.MirrorCS", {"start": v(-6096, -454.66) * mm, "end": v(-6019.6, -454.66) * mm});
            skLineSegment(sketch, "E400.MirrorCS", {"start": v(-6092.83, -448.3) * mm, "end": v(-6092.83, -227.33) * mm});
            skLineSegment(sketch, "E401.MirrorCS", {"start": v(-6019.6, -454.66) * mm, "end": v(-6019.6, -448.3) * mm});
            skLineSegment(sketch, "E402.MirrorCS", {"start": v(-6019.6, -448.3) * mm, "end": v(-6092.83, -448.3) * mm});
            skLineSegment(sketch, "E403.MirrorCS", {"start": v(-6172.4, -454.66) * mm, "end": v(-6172.4, -448.3) * mm});
            skLineSegment(sketch, "E404.MirrorCS", {"start": v(-6096, -454.66) * mm, "end": v(-6172.4, -454.66) * mm});
            skLineSegment(sketch, "E405", {"start": v(-6099.18, -6.35) * mm, "end": v(-6092.83, -6.35) * mm, "construction": true});
            skSolve(sketch);
        }
        {
            var Q0;
            Q0=qCreatedBy(makeId("Front.planeOp"),FACE);
            var sketch = newSketch(context, id + "F9", { "sketchPlane" : qUnion([Q0])});
            skLineSegment(sketch, "E406.0", {"start": v(7137.4, 0) * mm, "end": v(7493, 0) * mm, "construction": true});
            skLineSegment(sketch, "E407", {"start": v(7315.2, 0) * mm, "end": v(7315.2, -154.5) * mm, "construction": true});
            skLineSegment(sketch, "E408", {"start": v(7315.2, -154.5) * mm, "end": v(0, 0) * mm});
            skLineSegment(sketch, "E409.0", {"start": v(-177.8, 0) * mm, "end": v(177.8, 0) * mm, "construction": true});
            skSolve(sketch);
        }
        {
            var Q0;
            Q0 = qSketchRegion(id + "F8", true);
            var Q1;
            Q1 = qConstructionFilter(qBodyType(qCreatedBy(id + "F9" ,EDGE), BodyType.WIRE), ConstructionObject.NO);
            sweep(context, id + "F10", {"profiles" : qUnion([Q0]), "path" : qUnion([Q1])});
        }
        {
            var Q0;
            Q0=makeQuery(id+"F3.opExtrude","SWEPT_FACE",FACE,{"disambiguationData":[OSD([sQuery(id+"F2.wireOp",EDGE,"E134"),sQuery(id+"F2.wireOp",EDGE,"E140.MirrorCS")])]});
            var sketch = newSketch(context, id + "F11", { "sketchPlane" : qUnion([Q0])});
            skLineSegment(sketch, "E410.0", {"start": v(177.8, 0) * mm, "end": v(-177.8, 0) * mm, "construction": true});
            skPoint(sketch, "E411", {"position": v(0, 0) * mm});
            skLineSegment(sketch, "E412", {"start": v(0, 0) * mm, "end": v(-2832.1, 0) * mm, "construction": true});
            skLineSegment(sketch, "E413", {"start": v(-2832.1, 0) * mm, "end": v(-4711.7, 0) * mm, "construction": true});
            skLineSegment(sketch, "E414", {"start": v(-2832.1, -129.16) * mm, "end": v(-2832.1, 0) * mm, "construction": true});
            skLineSegment(sketch, "E415", {"start": v(-2832.1, -129.16) * mm, "end": v(-2835.27, -129.16) * mm, "construction": true});
            skLineSegment(sketch, "E416", {"start": v(-2832.1, 0) * mm, "end": v(-2905.12, 0) * mm});
            skLineSegment(sketch, "E417", {"start": v(-2905.12, 0) * mm, "end": v(-2905.12, -6.35) * mm});
            skLineSegment(sketch, "E418", {"start": v(-2905.12, -6.35) * mm, "end": v(-2835.27, -6.35) * mm});
            skLineSegment(sketch, "E419", {"start": v(-2835.27, -6.35) * mm, "end": v(-2835.27, -129.16) * mm});
            skLineSegment(sketch, "E420.MirrorCS", {"start": v(-2759.08, 0) * mm, "end": v(-2759.08, -6.35) * mm});
            skLineSegment(sketch, "E421.MirrorCS", {"start": v(-2832.1, 0) * mm, "end": v(-2759.08, 0) * mm});
            skLineSegment(sketch, "E422.MirrorCS", {"start": v(-2828.93, -6.35) * mm, "end": v(-2828.93, -129.16) * mm});
            skLineSegment(sketch, "E423.MirrorCS", {"start": v(-2759.08, -6.35) * mm, "end": v(-2828.92, -6.35) * mm});
            skLineSegment(sketch, "E424.MirrorCS", {"start": v(-2905.12, -251.97) * mm, "end": v(-2835.28, -251.97) * mm});
            skLineSegment(sketch, "E425.MirrorCS", {"start": v(-2835.27, -251.97) * mm, "end": v(-2835.27, -129.16) * mm});
            skLineSegment(sketch, "E426.MirrorCS", {"start": v(-2832.1, -258.32) * mm, "end": v(-2759.08, -258.32) * mm});
            skLineSegment(sketch, "E427.MirrorCS", {"start": v(-2828.93, -251.97) * mm, "end": v(-2828.93, -129.16) * mm});
            skLineSegment(sketch, "E428.MirrorCS", {"start": v(-2759.08, -258.32) * mm, "end": v(-2759.08, -251.97) * mm});
            skLineSegment(sketch, "E429.MirrorCS", {"start": v(-2759.08, -251.97) * mm, "end": v(-2828.92, -251.97) * mm});
            skLineSegment(sketch, "E430.MirrorCS", {"start": v(-2905.12, -258.32) * mm, "end": v(-2905.12, -251.97) * mm});
            skLineSegment(sketch, "E431.MirrorCS", {"start": v(-2832.1, -258.32) * mm, "end": v(-2905.12, -258.32) * mm});
            skLineSegment(sketch, "E432", {"start": v(-2835.27, -6.35) * mm, "end": v(-2828.92, -6.35) * mm, "construction": true});
            skPoint(sketch, "E433", {"position": v(-2832.1, 0) * mm});
            skLineSegment(sketch, "E434", {"start": v(-4711.7, -129.16) * mm, "end": v(-4711.7, 0) * mm, "construction": true});
            skLineSegment(sketch, "E435", {"start": v(-4711.7, -129.16) * mm, "end": v(-4714.88, -129.16) * mm, "construction": true});
            skLineSegment(sketch, "E436", {"start": v(-4711.7, 0) * mm, "end": v(-4784.73, 0) * mm});
            skLineSegment(sketch, "E437", {"start": v(-4784.73, 0) * mm, "end": v(-4784.73, -6.35) * mm});
            skLineSegment(sketch, "E438", {"start": v(-4784.73, -6.35) * mm, "end": v(-4714.88, -6.35) * mm});
            skLineSegment(sketch, "E439", {"start": v(-4714.88, -6.35) * mm, "end": v(-4714.88, -129.16) * mm});
            skLineSegment(sketch, "E440.MirrorCS", {"start": v(-4638.68, 0) * mm, "end": v(-4638.68, -6.35) * mm});
            skLineSegment(sketch, "E441.MirrorCS", {"start": v(-4711.7, 0) * mm, "end": v(-4638.68, 0) * mm});
            skLineSegment(sketch, "E442.MirrorCS", {"start": v(-4708.53, -6.35) * mm, "end": v(-4708.53, -129.16) * mm});
            skLineSegment(sketch, "E443.MirrorCS", {"start": v(-4638.68, -6.35) * mm, "end": v(-4708.52, -6.35) * mm});
            skLineSegment(sketch, "E444.MirrorCS", {"start": v(-4784.73, -251.97) * mm, "end": v(-4714.88, -251.97) * mm});
            skLineSegment(sketch, "E445.MirrorCS", {"start": v(-4714.88, -251.97) * mm, "end": v(-4714.88, -129.16) * mm});
            skLineSegment(sketch, "E446.MirrorCS", {"start": v(-4711.7, -258.32) * mm, "end": v(-4638.68, -258.32) * mm});
            skLineSegment(sketch, "E447.MirrorCS", {"start": v(-4708.53, -251.97) * mm, "end": v(-4708.53, -129.16) * mm});
            skLineSegment(sketch, "E448.MirrorCS", {"start": v(-4638.68, -258.32) * mm, "end": v(-4638.68, -251.97) * mm});
            skLineSegment(sketch, "E449.MirrorCS", {"start": v(-4638.68, -251.97) * mm, "end": v(-4708.52, -251.97) * mm});
            skLineSegment(sketch, "E450.MirrorCS", {"start": v(-4784.73, -258.32) * mm, "end": v(-4784.73, -251.97) * mm});
            skLineSegment(sketch, "E451.MirrorCS", {"start": v(-4711.7, -258.32) * mm, "end": v(-4784.73, -258.32) * mm});
            skLineSegment(sketch, "E452", {"start": v(-4714.88, -6.35) * mm, "end": v(-4708.52, -6.35) * mm, "construction": true});
            skPoint(sketch, "E453", {"position": v(-4711.7, 0) * mm});
            skSolve(sketch);
        }
        {
            var Q0;
            Q0 = qSketchRegion(id + "F11", true);
            var Q1;
            Q1=makeQuery(id+"F3.opExtrude","SWEPT_FACE",FACE,{"disambiguationData":[OSD([sQuery(id+"F2.wireOp",EDGE,"E94"),sQuery(id+"F2.wireOp",EDGE,"E100.MirrorCS")])]});
            extrude(context, id + "F12", {"entities" : qUnion([Q0]), "endBound" : BoundingType.UP_TO_SURFACE, "oppositeDirection" : true, "endBoundEntityFace" : qUnion([Q1]), "depth" : 25.4 * mm});
        }
        {
            var Q0;
            Q0=makeQuery(id+"F3.opExtrude","SWEPT_FACE",FACE,{"disambiguationData":[OSD([sQuery(id+"F2.wireOp",EDGE,"E111"),sQuery(id+"F2.wireOp",EDGE,"E116.MirrorCS")])]});
            var sketch = newSketch(context, id + "F13", { "sketchPlane" : qUnion([Q0])});
            skLineSegment(sketch, "E454.0", {"start": v(-4638.68, -3406.77) * mm, "end": v(-4638.68, -6099.18) * mm, "construction": true});
            skLineSegment(sketch, "E455.0", {"start": v(-7315.2, -4676.78) * mm, "end": v(0, -4676.78) * mm, "construction": true});
            skLineSegment(sketch, "E456.0", {"start": v(-7315.2, -4822.82) * mm, "end": v(0, -4822.82) * mm, "construction": true});
            skLineSegment(sketch, "E457.0", {"start": v(-2905.12, -3406.77) * mm, "end": v(-2905.12, -6099.18) * mm, "construction": true});
            skLineSegment(sketch, "E458.bottom", {"start": v(-4638.68, -4676.78) * mm, "end": v(-2905.12, -4676.78) * mm});
            skLineSegment(sketch, "E458.top", {"start": v(-4638.68, -4822.83) * mm, "end": v(-2905.12, -4822.83) * mm});
            skLineSegment(sketch, "E458.left", {"start": v(-4638.68, -4676.78) * mm, "end": v(-4638.68, -4822.82) * mm});
            skLineSegment(sketch, "E458.right", {"start": v(-2905.12, -4676.78) * mm, "end": v(-2905.12, -4822.83) * mm});
            skSolve(sketch);
        }
        {
            var Q0;
            Q0=makeQuery(id+"F13.imprint","IMPRINT",FACE,{"disambiguationData":[TD([[makeQuery(id+"F13.imprint","IMPRINT",EDGE,{"derivedFrom":sQuery(id+"F13.wireOp",EDGE,"E458.bottom")}),-1.0]])]});
            var Q1;
            Q1=makeQuery(id+"F3.opExtrude","SWEPT_FACE",FACE,{"disambiguationData":[OSD([sQuery(id+"F2.wireOp",EDGE,"E121.MirrorCS"),sQuery(id+"F2.wireOp",EDGE,"E126.MirrorCS")])]});
            extrude(context, id + "F14", {"entities" : qUnion([Q0]), "operationType" : NewBodyOperationType.REMOVE, "endBound" : BoundingType.UP_TO_SURFACE, "oppositeDirection" : true, "endBoundEntityFace" : qUnion([Q1]), "depth" : 25.4 * mm});
        }
        {
            var Q0;
            Q0=makeQuery(id+"F1.opExtrude","SWEPT_BODY",BODY,{"disambiguationData":[OSD([sQuery(id+"F0.wireOp",EDGE,"E2"),sQuery(id+"F0.wireOp",EDGE,"E3"),sQuery(id+"F0.wireOp",EDGE,"E4"),sQuery(id+"F0.wireOp",EDGE,"E5"),sQuery(id+"F0.wireOp",EDGE,"E6.MirrorCS"),sQuery(id+"F0.wireOp",EDGE,"E7.MirrorCS"),sQuery(id+"F0.wireOp",EDGE,"E8.MirrorCS"),sQuery(id+"F0.wireOp",EDGE,"E9.MirrorCS"),sQuery(id+"F0.wireOp",EDGE,"E10.MirrorCS"),sQuery(id+"F0.wireOp",EDGE,"E11.MirrorCS"),sQuery(id+"F0.wireOp",EDGE,"E12.MirrorCS"),sQuery(id+"F0.wireOp",EDGE,"E13.MirrorCS"),sQuery(id+"F0.wireOp",EDGE,"E14.MirrorCS"),sQuery(id+"F0.wireOp",EDGE,"E15.MirrorCS"),sQuery(id+"F0.wireOp",EDGE,"E16.MirrorCS"),sQuery(id+"F0.wireOp",EDGE,"E17.MirrorCS")])]});
            var Q1;
            Q1=makeQuery(id+"F1.opExtrude","SWEPT_BODY",BODY,{"disambiguationData":[OSD([sQuery(id+"F0.wireOp",EDGE,"E19.0.1.1"),sQuery(id+"F0.wireOp",EDGE,"E19.0.1.2"),sQuery(id+"F0.wireOp",EDGE,"E19.0.1.3"),sQuery(id+"F0.wireOp",EDGE,"E19.0.1.4"),sQuery(id+"F0.wireOp",EDGE,"E19.0.1.5"),sQuery(id+"F0.wireOp",EDGE,"E19.0.1.6"),sQuery(id+"F0.wireOp",EDGE,"E19.0.1.7"),sQuery(id+"F0.wireOp",EDGE,"E19.0.1.8"),sQuery(id+"F0.wireOp",EDGE,"E19.0.1.9"),sQuery(id+"F0.wireOp",EDGE,"E19.0.1.10"),sQuery(id+"F0.wireOp",EDGE,"E19.0.1.11"),sQuery(id+"F0.wireOp",EDGE,"E19.0.1.12"),sQuery(id+"F0.wireOp",EDGE,"E19.0.1.13"),sQuery(id+"F0.wireOp",EDGE,"E19.0.1.14"),sQuery(id+"F0.wireOp",EDGE,"E19.0.1.15"),sQuery(id+"F0.wireOp",EDGE,"E19.0.1.16")])]});
            var Q2;
            Q2=makeQuery(id+"F1.opExtrude","SWEPT_BODY",BODY,{"disambiguationData":[OSD([sQuery(id+"F0.wireOp",EDGE,"E19.1.0.1"),sQuery(id+"F0.wireOp",EDGE,"E19.1.0.2"),sQuery(id+"F0.wireOp",EDGE,"E19.1.0.3"),sQuery(id+"F0.wireOp",EDGE,"E19.1.0.4"),sQuery(id+"F0.wireOp",EDGE,"E19.1.0.5"),sQuery(id+"F0.wireOp",EDGE,"E19.1.0.6"),sQuery(id+"F0.wireOp",EDGE,"E19.1.0.7"),sQuery(id+"F0.wireOp",EDGE,"E19.1.0.8"),sQuery(id+"F0.wireOp",EDGE,"E19.1.0.9"),sQuery(id+"F0.wireOp",EDGE,"E19.1.0.10"),sQuery(id+"F0.wireOp",EDGE,"E19.1.0.11"),sQuery(id+"F0.wireOp",EDGE,"E19.1.0.12"),sQuery(id+"F0.wireOp",EDGE,"E19.1.0.13"),sQuery(id+"F0.wireOp",EDGE,"E19.1.0.14"),sQuery(id+"F0.wireOp",EDGE,"E19.1.0.15"),sQuery(id+"F0.wireOp",EDGE,"E19.1.0.16")])]});
            var Q3;
            Q3=makeQuery(id+"F1.opExtrude","SWEPT_BODY",BODY,{"disambiguationData":[OSD([sQuery(id+"F0.wireOp",EDGE,"E19.1.1.1"),sQuery(id+"F0.wireOp",EDGE,"E19.1.1.2"),sQuery(id+"F0.wireOp",EDGE,"E19.1.1.3"),sQuery(id+"F0.wireOp",EDGE,"E19.1.1.4"),sQuery(id+"F0.wireOp",EDGE,"E19.1.1.5"),sQuery(id+"F0.wireOp",EDGE,"E19.1.1.6"),sQuery(id+"F0.wireOp",EDGE,"E19.1.1.7"),sQuery(id+"F0.wireOp",EDGE,"E19.1.1.8"),sQuery(id+"F0.wireOp",EDGE,"E19.1.1.9"),sQuery(id+"F0.wireOp",EDGE,"E19.1.1.10"),sQuery(id+"F0.wireOp",EDGE,"E19.1.1.11"),sQuery(id+"F0.wireOp",EDGE,"E19.1.1.12"),sQuery(id+"F0.wireOp",EDGE,"E19.1.1.13"),sQuery(id+"F0.wireOp",EDGE,"E19.1.1.14"),sQuery(id+"F0.wireOp",EDGE,"E19.1.1.15"),sQuery(id+"F0.wireOp",EDGE,"E19.1.1.16")])]});
            var Q4;
            Q4=makeQuery(id+"F1.opExtrude","SWEPT_BODY",BODY,{"disambiguationData":[OSD([sQuery(id+"F0.wireOp",EDGE,"E20.1.0.0"),sQuery(id+"F0.wireOp",EDGE,"E20.1.0.1"),sQuery(id+"F0.wireOp",EDGE,"E20.1.0.2"),sQuery(id+"F0.wireOp",EDGE,"E20.1.0.3"),sQuery(id+"F0.wireOp",EDGE,"E20.1.0.5"),sQuery(id+"F0.wireOp",EDGE,"E20.1.0.6"),sQuery(id+"F0.wireOp",EDGE,"E20.1.0.7"),sQuery(id+"F0.wireOp",EDGE,"E20.1.0.8"),sQuery(id+"F0.wireOp",EDGE,"E20.1.0.9"),sQuery(id+"F0.wireOp",EDGE,"E20.1.0.10"),sQuery(id+"F0.wireOp",EDGE,"E20.1.0.11"),sQuery(id+"F0.wireOp",EDGE,"E20.1.0.12"),sQuery(id+"F0.wireOp",EDGE,"E20.1.0.13"),sQuery(id+"F0.wireOp",EDGE,"E20.1.0.14"),sQuery(id+"F0.wireOp",EDGE,"E20.1.0.15"),sQuery(id+"F0.wireOp",EDGE,"E20.1.0.17")])]});
            var Q5;
            Q5=makeQuery(id+"F1.opExtrude","SWEPT_BODY",BODY,{"disambiguationData":[OSD([sQuery(id+"F0.wireOp",EDGE,"E20.1.0.19"),sQuery(id+"F0.wireOp",EDGE,"E20.1.0.20"),sQuery(id+"F0.wireOp",EDGE,"E20.1.0.22"),sQuery(id+"F0.wireOp",EDGE,"E20.1.0.23"),sQuery(id+"F0.wireOp",EDGE,"E20.1.0.24"),sQuery(id+"F0.wireOp",EDGE,"E20.1.0.25"),sQuery(id+"F0.wireOp",EDGE,"E20.1.0.26"),sQuery(id+"F0.wireOp",EDGE,"E20.1.0.27"),sQuery(id+"F0.wireOp",EDGE,"E20.1.0.28"),sQuery(id+"F0.wireOp",EDGE,"E20.1.0.29"),sQuery(id+"F0.wireOp",EDGE,"E20.1.0.30"),sQuery(id+"F0.wireOp",EDGE,"E20.1.0.31"),sQuery(id+"F0.wireOp",EDGE,"E20.1.0.32"),sQuery(id+"F0.wireOp",EDGE,"E20.1.0.33"),sQuery(id+"F0.wireOp",EDGE,"E20.1.0.34"),sQuery(id+"F0.wireOp",EDGE,"E20.1.0.35")])]});
            var Q6;
            Q6=makeQuery(id+"F3.opExtrude","SWEPT_BODY",BODY,{"disambiguationData":[OSD([sQuery(id+"F2.wireOp",EDGE,"E23"),sQuery(id+"F2.wireOp",EDGE,"E24"),sQuery(id+"F2.wireOp",EDGE,"E25"),sQuery(id+"F2.wireOp",EDGE,"E26"),sQuery(id+"F2.wireOp",EDGE,"E27.MirrorCS"),sQuery(id+"F2.wireOp",EDGE,"E28.MirrorCS"),sQuery(id+"F2.wireOp",EDGE,"E29.MirrorCS"),sQuery(id+"F2.wireOp",EDGE,"E30.MirrorCS"),sQuery(id+"F2.wireOp",EDGE,"E31.MirrorCS"),sQuery(id+"F2.wireOp",EDGE,"E32.MirrorCS"),sQuery(id+"F2.wireOp",EDGE,"E33.MirrorCS"),sQuery(id+"F2.wireOp",EDGE,"E34.MirrorCS"),sQuery(id+"F2.wireOp",EDGE,"E35.MirrorCS"),sQuery(id+"F2.wireOp",EDGE,"E36.MirrorCS"),sQuery(id+"F2.wireOp",EDGE,"E37.MirrorCS"),sQuery(id+"F2.wireOp",EDGE,"E38.MirrorCS")])]});
            var Q7;
            Q7=makeQuery(id+"F3.opExtrude","SWEPT_BODY",BODY,{"disambiguationData":[OSD([sQuery(id+"F2.wireOp",EDGE,"E51"),sQuery(id+"F2.wireOp",EDGE,"E52"),sQuery(id+"F2.wireOp",EDGE,"E53"),sQuery(id+"F2.wireOp",EDGE,"E54"),sQuery(id+"F2.wireOp",EDGE,"E55.MirrorCS"),sQuery(id+"F2.wireOp",EDGE,"E56.MirrorCS"),sQuery(id+"F2.wireOp",EDGE,"E57.MirrorCS"),sQuery(id+"F2.wireOp",EDGE,"E58.MirrorCS"),sQuery(id+"F2.wireOp",EDGE,"E59.MirrorCS"),sQuery(id+"F2.wireOp",EDGE,"E60.MirrorCS"),sQuery(id+"F2.wireOp",EDGE,"E61.MirrorCS"),sQuery(id+"F2.wireOp",EDGE,"E62.MirrorCS"),sQuery(id+"F2.wireOp",EDGE,"E63.MirrorCS"),sQuery(id+"F2.wireOp",EDGE,"E64.MirrorCS"),sQuery(id+"F2.wireOp",EDGE,"E65.MirrorCS"),sQuery(id+"F2.wireOp",EDGE,"E66.MirrorCS")])]});
            var Q8;
            Q8=makeQuery(id+"F3.opExtrude","SWEPT_BODY",BODY,{"disambiguationData":[OSD([sQuery(id+"F2.wireOp",EDGE,"E71"),sQuery(id+"F2.wireOp",EDGE,"E72"),sQuery(id+"F2.wireOp",EDGE,"E73"),sQuery(id+"F2.wireOp",EDGE,"E74"),sQuery(id+"F2.wireOp",EDGE,"E75.MirrorCS"),sQuery(id+"F2.wireOp",EDGE,"E76.MirrorCS"),sQuery(id+"F2.wireOp",EDGE,"E77.MirrorCS"),sQuery(id+"F2.wireOp",EDGE,"E78.MirrorCS"),sQuery(id+"F2.wireOp",EDGE,"E79.MirrorCS"),sQuery(id+"F2.wireOp",EDGE,"E80.MirrorCS"),sQuery(id+"F2.wireOp",EDGE,"E81.MirrorCS"),sQuery(id+"F2.wireOp",EDGE,"E82.MirrorCS"),sQuery(id+"F2.wireOp",EDGE,"E83.MirrorCS"),sQuery(id+"F2.wireOp",EDGE,"E84.MirrorCS"),sQuery(id+"F2.wireOp",EDGE,"E85.MirrorCS"),sQuery(id+"F2.wireOp",EDGE,"E86.MirrorCS")])]});
            var Q9;
            Q9=makeQuery(id+"F3.opExtrude","SWEPT_BODY",BODY,{"disambiguationData":[OSD([sQuery(id+"F2.wireOp",EDGE,"E91"),sQuery(id+"F2.wireOp",EDGE,"E92"),sQuery(id+"F2.wireOp",EDGE,"E93"),sQuery(id+"F2.wireOp",EDGE,"E94"),sQuery(id+"F2.wireOp",EDGE,"E95.MirrorCS"),sQuery(id+"F2.wireOp",EDGE,"E96.MirrorCS"),sQuery(id+"F2.wireOp",EDGE,"E97.MirrorCS"),sQuery(id+"F2.wireOp",EDGE,"E98.MirrorCS"),sQuery(id+"F2.wireOp",EDGE,"E99.MirrorCS"),sQuery(id+"F2.wireOp",EDGE,"E100.MirrorCS"),sQuery(id+"F2.wireOp",EDGE,"E101.MirrorCS"),sQuery(id+"F2.wireOp",EDGE,"E102.MirrorCS"),sQuery(id+"F2.wireOp",EDGE,"E103.MirrorCS"),sQuery(id+"F2.wireOp",EDGE,"E104.MirrorCS"),sQuery(id+"F2.wireOp",EDGE,"E105.MirrorCS"),sQuery(id+"F2.wireOp",EDGE,"E106.MirrorCS")])]});
            var Q10;
            Q10=makeQuery(id+"F3.opExtrude","SWEPT_BODY",BODY,{"disambiguationData":[OSD([sQuery(id+"F2.wireOp",EDGE,"E131"),sQuery(id+"F2.wireOp",EDGE,"E132"),sQuery(id+"F2.wireOp",EDGE,"E133"),sQuery(id+"F2.wireOp",EDGE,"E134"),sQuery(id+"F2.wireOp",EDGE,"E135.MirrorCS"),sQuery(id+"F2.wireOp",EDGE,"E136.MirrorCS"),sQuery(id+"F2.wireOp",EDGE,"E137.MirrorCS"),sQuery(id+"F2.wireOp",EDGE,"E138.MirrorCS"),sQuery(id+"F2.wireOp",EDGE,"E139.MirrorCS"),sQuery(id+"F2.wireOp",EDGE,"E140.MirrorCS"),sQuery(id+"F2.wireOp",EDGE,"E141.MirrorCS"),sQuery(id+"F2.wireOp",EDGE,"E142.MirrorCS"),sQuery(id+"F2.wireOp",EDGE,"E143.MirrorCS"),sQuery(id+"F2.wireOp",EDGE,"E144.MirrorCS"),sQuery(id+"F2.wireOp",EDGE,"E145.MirrorCS"),sQuery(id+"F2.wireOp",EDGE,"E146.MirrorCS")])]});
            var Q11;
            Q11=makeQuery(id+"F3.opExtrude","SWEPT_BODY",BODY,{"disambiguationData":[OSD([sQuery(id+"F2.wireOp",EDGE,"E150"),sQuery(id+"F2.wireOp",EDGE,"E151"),sQuery(id+"F2.wireOp",EDGE,"E152"),sQuery(id+"F2.wireOp",EDGE,"E153"),sQuery(id+"F2.wireOp",EDGE,"E154.MirrorCS"),sQuery(id+"F2.wireOp",EDGE,"E155.MirrorCS"),sQuery(id+"F2.wireOp",EDGE,"E156.MirrorCS"),sQuery(id+"F2.wireOp",EDGE,"E157.MirrorCS"),sQuery(id+"F2.wireOp",EDGE,"E158.MirrorCS"),sQuery(id+"F2.wireOp",EDGE,"E159.MirrorCS"),sQuery(id+"F2.wireOp",EDGE,"E160.MirrorCS"),sQuery(id+"F2.wireOp",EDGE,"E161.MirrorCS"),sQuery(id+"F2.wireOp",EDGE,"E162.MirrorCS"),sQuery(id+"F2.wireOp",EDGE,"E163.MirrorCS"),sQuery(id+"F2.wireOp",EDGE,"E164.MirrorCS"),sQuery(id+"F2.wireOp",EDGE,"E165.MirrorCS")])]});
            var Q12;
            Q12=makeQuery(id+"F5.opExtrude","SWEPT_BODY",BODY,{"disambiguationData":[OSD([sQuery(id+"F4.wireOp",EDGE,"E174"),sQuery(id+"F4.wireOp",EDGE,"E175"),sQuery(id+"F4.wireOp",EDGE,"E176"),sQuery(id+"F4.wireOp",EDGE,"E177"),sQuery(id+"F4.wireOp",EDGE,"E178.MirrorCS"),sQuery(id+"F4.wireOp",EDGE,"E179.MirrorCS"),sQuery(id+"F4.wireOp",EDGE,"E180.MirrorCS"),sQuery(id+"F4.wireOp",EDGE,"E181.MirrorCS"),sQuery(id+"F4.wireOp",EDGE,"E182.MirrorCS"),sQuery(id+"F4.wireOp",EDGE,"E183.MirrorCS"),sQuery(id+"F4.wireOp",EDGE,"E184.MirrorCS"),sQuery(id+"F4.wireOp",EDGE,"E185.MirrorCS"),sQuery(id+"F4.wireOp",EDGE,"E186.MirrorCS"),sQuery(id+"F4.wireOp",EDGE,"E187.MirrorCS"),sQuery(id+"F4.wireOp",EDGE,"E188.MirrorCS"),sQuery(id+"F4.wireOp",EDGE,"E189.MirrorCS")])]});
            var Q13;
            Q13=makeQuery(id+"F7.opExtrude","SWEPT_BODY",BODY,{"disambiguationData":[OSD([sQuery(id+"F6.wireOp",EDGE,"E207"),sQuery(id+"F6.wireOp",EDGE,"E208"),sQuery(id+"F6.wireOp",EDGE,"E209"),sQuery(id+"F6.wireOp",EDGE,"E210"),sQuery(id+"F6.wireOp",EDGE,"E211.MirrorCS"),sQuery(id+"F6.wireOp",EDGE,"E212.MirrorCS"),sQuery(id+"F6.wireOp",EDGE,"E213.MirrorCS"),sQuery(id+"F6.wireOp",EDGE,"E214.MirrorCS"),sQuery(id+"F6.wireOp",EDGE,"E215.MirrorCS"),sQuery(id+"F6.wireOp",EDGE,"E216.MirrorCS"),sQuery(id+"F6.wireOp",EDGE,"E217.MirrorCS"),sQuery(id+"F6.wireOp",EDGE,"E218.MirrorCS"),sQuery(id+"F6.wireOp",EDGE,"E219.MirrorCS"),sQuery(id+"F6.wireOp",EDGE,"E220.MirrorCS"),sQuery(id+"F6.wireOp",EDGE,"E221.MirrorCS"),sQuery(id+"F6.wireOp",EDGE,"E222.MirrorCS")])]});
            var Q14;
            Q14=makeQuery(id+"F7.opExtrude","SWEPT_BODY",BODY,{"disambiguationData":[OSD([sQuery(id+"F6.wireOp",EDGE,"E227"),sQuery(id+"F6.wireOp",EDGE,"E228"),sQuery(id+"F6.wireOp",EDGE,"E229"),sQuery(id+"F6.wireOp",EDGE,"E230"),sQuery(id+"F6.wireOp",EDGE,"E231.MirrorCS"),sQuery(id+"F6.wireOp",EDGE,"E232.MirrorCS"),sQuery(id+"F6.wireOp",EDGE,"E233.MirrorCS"),sQuery(id+"F6.wireOp",EDGE,"E234.MirrorCS"),sQuery(id+"F6.wireOp",EDGE,"E235.MirrorCS"),sQuery(id+"F6.wireOp",EDGE,"E236.MirrorCS"),sQuery(id+"F6.wireOp",EDGE,"E237.MirrorCS"),sQuery(id+"F6.wireOp",EDGE,"E238.MirrorCS"),sQuery(id+"F6.wireOp",EDGE,"E239.MirrorCS"),sQuery(id+"F6.wireOp",EDGE,"E240.MirrorCS"),sQuery(id+"F6.wireOp",EDGE,"E241.MirrorCS"),sQuery(id+"F6.wireOp",EDGE,"E242.MirrorCS")])]});
            var Q15;
            Q15=makeQuery(id+"F7.opExtrude","SWEPT_BODY",BODY,{"disambiguationData":[OSD([sQuery(id+"F6.wireOp",EDGE,"E247"),sQuery(id+"F6.wireOp",EDGE,"E248"),sQuery(id+"F6.wireOp",EDGE,"E249"),sQuery(id+"F6.wireOp",EDGE,"E250"),sQuery(id+"F6.wireOp",EDGE,"E251.MirrorCS"),sQuery(id+"F6.wireOp",EDGE,"E252.MirrorCS"),sQuery(id+"F6.wireOp",EDGE,"E253.MirrorCS"),sQuery(id+"F6.wireOp",EDGE,"E254.MirrorCS"),sQuery(id+"F6.wireOp",EDGE,"E255.MirrorCS"),sQuery(id+"F6.wireOp",EDGE,"E256.MirrorCS"),sQuery(id+"F6.wireOp",EDGE,"E257.MirrorCS"),sQuery(id+"F6.wireOp",EDGE,"E258.MirrorCS"),sQuery(id+"F6.wireOp",EDGE,"E259.MirrorCS"),sQuery(id+"F6.wireOp",EDGE,"E260.MirrorCS"),sQuery(id+"F6.wireOp",EDGE,"E261.MirrorCS"),sQuery(id+"F6.wireOp",EDGE,"E262.MirrorCS")])]});
            var Q16;
            Q16=makeQuery(id+"F7.opExtrude","SWEPT_BODY",BODY,{"disambiguationData":[OSD([sQuery(id+"F6.wireOp",EDGE,"E267"),sQuery(id+"F6.wireOp",EDGE,"E268"),sQuery(id+"F6.wireOp",EDGE,"E269"),sQuery(id+"F6.wireOp",EDGE,"E270"),sQuery(id+"F6.wireOp",EDGE,"E271.MirrorCS"),sQuery(id+"F6.wireOp",EDGE,"E272.MirrorCS"),sQuery(id+"F6.wireOp",EDGE,"E273.MirrorCS"),sQuery(id+"F6.wireOp",EDGE,"E274.MirrorCS"),sQuery(id+"F6.wireOp",EDGE,"E275.MirrorCS"),sQuery(id+"F6.wireOp",EDGE,"E276.MirrorCS"),sQuery(id+"F6.wireOp",EDGE,"E277.MirrorCS"),sQuery(id+"F6.wireOp",EDGE,"E278.MirrorCS"),sQuery(id+"F6.wireOp",EDGE,"E279.MirrorCS"),sQuery(id+"F6.wireOp",EDGE,"E280.MirrorCS"),sQuery(id+"F6.wireOp",EDGE,"E281.MirrorCS"),sQuery(id+"F6.wireOp",EDGE,"E282.MirrorCS")])]});
            var Q17;
            Q17=makeQuery(id+"F7.opExtrude","SWEPT_BODY",BODY,{"disambiguationData":[OSD([sQuery(id+"F6.wireOp",EDGE,"E287"),sQuery(id+"F6.wireOp",EDGE,"E288"),sQuery(id+"F6.wireOp",EDGE,"E289"),sQuery(id+"F6.wireOp",EDGE,"E290"),sQuery(id+"F6.wireOp",EDGE,"E291.MirrorCS"),sQuery(id+"F6.wireOp",EDGE,"E292.MirrorCS"),sQuery(id+"F6.wireOp",EDGE,"E293.MirrorCS"),sQuery(id+"F6.wireOp",EDGE,"E294.MirrorCS"),sQuery(id+"F6.wireOp",EDGE,"E295.MirrorCS"),sQuery(id+"F6.wireOp",EDGE,"E296.MirrorCS"),sQuery(id+"F6.wireOp",EDGE,"E297.MirrorCS"),sQuery(id+"F6.wireOp",EDGE,"E298.MirrorCS"),sQuery(id+"F6.wireOp",EDGE,"E299.MirrorCS"),sQuery(id+"F6.wireOp",EDGE,"E300.MirrorCS"),sQuery(id+"F6.wireOp",EDGE,"E301.MirrorCS"),sQuery(id+"F6.wireOp",EDGE,"E302.MirrorCS")])]});
            var Q18;
            Q18=makeQuery(id+"F7.opExtrude","SWEPT_BODY",BODY,{"disambiguationData":[OSD([sQuery(id+"F6.wireOp",EDGE,"E308"),sQuery(id+"F6.wireOp",EDGE,"E309"),sQuery(id+"F6.wireOp",EDGE,"E310"),sQuery(id+"F6.wireOp",EDGE,"E311"),sQuery(id+"F6.wireOp",EDGE,"E312.MirrorCS"),sQuery(id+"F6.wireOp",EDGE,"E313.MirrorCS"),sQuery(id+"F6.wireOp",EDGE,"E314.MirrorCS"),sQuery(id+"F6.wireOp",EDGE,"E315.MirrorCS"),sQuery(id+"F6.wireOp",EDGE,"E316.MirrorCS"),sQuery(id+"F6.wireOp",EDGE,"E317.MirrorCS"),sQuery(id+"F6.wireOp",EDGE,"E318.MirrorCS"),sQuery(id+"F6.wireOp",EDGE,"E319.MirrorCS"),sQuery(id+"F6.wireOp",EDGE,"E320.MirrorCS"),sQuery(id+"F6.wireOp",EDGE,"E321.MirrorCS"),sQuery(id+"F6.wireOp",EDGE,"E322.MirrorCS"),sQuery(id+"F6.wireOp",EDGE,"E323.MirrorCS")])]});
            var Q19;
            Q19=makeQuery(id+"F7.opExtrude","SWEPT_BODY",BODY,{"disambiguationData":[OSD([sQuery(id+"F6.wireOp",EDGE,"E328"),sQuery(id+"F6.wireOp",EDGE,"E329"),sQuery(id+"F6.wireOp",EDGE,"E330"),sQuery(id+"F6.wireOp",EDGE,"E331"),sQuery(id+"F6.wireOp",EDGE,"E332.MirrorCS"),sQuery(id+"F6.wireOp",EDGE,"E333.MirrorCS"),sQuery(id+"F6.wireOp",EDGE,"E334.MirrorCS"),sQuery(id+"F6.wireOp",EDGE,"E335.MirrorCS"),sQuery(id+"F6.wireOp",EDGE,"E336.MirrorCS"),sQuery(id+"F6.wireOp",EDGE,"E337.MirrorCS"),sQuery(id+"F6.wireOp",EDGE,"E338.MirrorCS"),sQuery(id+"F6.wireOp",EDGE,"E339.MirrorCS"),sQuery(id+"F6.wireOp",EDGE,"E340.MirrorCS"),sQuery(id+"F6.wireOp",EDGE,"E341.MirrorCS"),sQuery(id+"F6.wireOp",EDGE,"E342.MirrorCS"),sQuery(id+"F6.wireOp",EDGE,"E343.MirrorCS")])]});
            var Q20;
            Q20=makeQuery(id+"F7.opExtrude","SWEPT_BODY",BODY,{"disambiguationData":[OSD([sQuery(id+"F6.wireOp",EDGE,"E347"),sQuery(id+"F6.wireOp",EDGE,"E348"),sQuery(id+"F6.wireOp",EDGE,"E349"),sQuery(id+"F6.wireOp",EDGE,"E350"),sQuery(id+"F6.wireOp",EDGE,"E351.MirrorCS"),sQuery(id+"F6.wireOp",EDGE,"E352.MirrorCS"),sQuery(id+"F6.wireOp",EDGE,"E353.MirrorCS"),sQuery(id+"F6.wireOp",EDGE,"E354.MirrorCS"),sQuery(id+"F6.wireOp",EDGE,"E355.MirrorCS"),sQuery(id+"F6.wireOp",EDGE,"E356.MirrorCS"),sQuery(id+"F6.wireOp",EDGE,"E357.MirrorCS"),sQuery(id+"F6.wireOp",EDGE,"E358.MirrorCS"),sQuery(id+"F6.wireOp",EDGE,"E359.MirrorCS"),sQuery(id+"F6.wireOp",EDGE,"E360.MirrorCS"),sQuery(id+"F6.wireOp",EDGE,"E361.MirrorCS"),sQuery(id+"F6.wireOp",EDGE,"E362.MirrorCS")])]});
            var Q21;
            Q21=makeQuery(id+"F10.opSweep","SWEPT_BODY",BODY,{"disambiguationData":[OSD([sQuery(id+"F8.wireOp",EDGE,"E370"),sQuery(id+"F8.wireOp",EDGE,"E371"),sQuery(id+"F8.wireOp",EDGE,"E372"),sQuery(id+"F8.wireOp",EDGE,"E373"),sQuery(id+"F8.wireOp",EDGE,"E374.MirrorCS"),sQuery(id+"F8.wireOp",EDGE,"E375.MirrorCS"),sQuery(id+"F8.wireOp",EDGE,"E376.MirrorCS"),sQuery(id+"F8.wireOp",EDGE,"E377.MirrorCS"),sQuery(id+"F8.wireOp",EDGE,"E378.MirrorCS"),sQuery(id+"F8.wireOp",EDGE,"E379.MirrorCS"),sQuery(id+"F8.wireOp",EDGE,"E380.MirrorCS"),sQuery(id+"F8.wireOp",EDGE,"E381.MirrorCS"),sQuery(id+"F8.wireOp",EDGE,"E382.MirrorCS"),sQuery(id+"F8.wireOp",EDGE,"E383.MirrorCS"),sQuery(id+"F8.wireOp",EDGE,"E384.MirrorCS"),sQuery(id+"F8.wireOp",EDGE,"E385.MirrorCS"),sQuery(id+"F9.wireOp",EDGE,"E408")])]});
            var Q22;
            Q22=makeQuery(id+"F10.opSweep","SWEPT_BODY",BODY,{"disambiguationData":[OSD([sQuery(id+"F8.wireOp",EDGE,"E389"),sQuery(id+"F8.wireOp",EDGE,"E390"),sQuery(id+"F8.wireOp",EDGE,"E391"),sQuery(id+"F8.wireOp",EDGE,"E392"),sQuery(id+"F8.wireOp",EDGE,"E393.MirrorCS"),sQuery(id+"F8.wireOp",EDGE,"E394.MirrorCS"),sQuery(id+"F8.wireOp",EDGE,"E395.MirrorCS"),sQuery(id+"F8.wireOp",EDGE,"E396.MirrorCS"),sQuery(id+"F8.wireOp",EDGE,"E397.MirrorCS"),sQuery(id+"F8.wireOp",EDGE,"E398.MirrorCS"),sQuery(id+"F8.wireOp",EDGE,"E399.MirrorCS"),sQuery(id+"F8.wireOp",EDGE,"E400.MirrorCS"),sQuery(id+"F8.wireOp",EDGE,"E401.MirrorCS"),sQuery(id+"F8.wireOp",EDGE,"E402.MirrorCS"),sQuery(id+"F8.wireOp",EDGE,"E403.MirrorCS"),sQuery(id+"F8.wireOp",EDGE,"E404.MirrorCS"),sQuery(id+"F9.wireOp",EDGE,"E408")])]});
            var Q23;
            Q23=makeQuery(id+"F12.opExtrude","SWEPT_BODY",BODY,{"disambiguationData":[OSD([sQuery(id+"F11.wireOp",EDGE,"E416"),sQuery(id+"F11.wireOp",EDGE,"E417"),sQuery(id+"F11.wireOp",EDGE,"E418"),sQuery(id+"F11.wireOp",EDGE,"E419"),sQuery(id+"F11.wireOp",EDGE,"E420.MirrorCS"),sQuery(id+"F11.wireOp",EDGE,"E421.MirrorCS"),sQuery(id+"F11.wireOp",EDGE,"E422.MirrorCS"),sQuery(id+"F11.wireOp",EDGE,"E423.MirrorCS"),sQuery(id+"F11.wireOp",EDGE,"E424.MirrorCS"),sQuery(id+"F11.wireOp",EDGE,"E425.MirrorCS"),sQuery(id+"F11.wireOp",EDGE,"E426.MirrorCS"),sQuery(id+"F11.wireOp",EDGE,"E427.MirrorCS"),sQuery(id+"F11.wireOp",EDGE,"E428.MirrorCS"),sQuery(id+"F11.wireOp",EDGE,"E429.MirrorCS"),sQuery(id+"F11.wireOp",EDGE,"E430.MirrorCS"),sQuery(id+"F11.wireOp",EDGE,"E431.MirrorCS")])]});
            var Q24;
            Q24=makeQuery(id+"F12.opExtrude","SWEPT_BODY",BODY,{"disambiguationData":[OSD([sQuery(id+"F11.wireOp",EDGE,"E436"),sQuery(id+"F11.wireOp",EDGE,"E437"),sQuery(id+"F11.wireOp",EDGE,"E438"),sQuery(id+"F11.wireOp",EDGE,"E439"),sQuery(id+"F11.wireOp",EDGE,"E440.MirrorCS"),sQuery(id+"F11.wireOp",EDGE,"E441.MirrorCS"),sQuery(id+"F11.wireOp",EDGE,"E442.MirrorCS"),sQuery(id+"F11.wireOp",EDGE,"E443.MirrorCS"),sQuery(id+"F11.wireOp",EDGE,"E444.MirrorCS"),sQuery(id+"F11.wireOp",EDGE,"E445.MirrorCS"),sQuery(id+"F11.wireOp",EDGE,"E446.MirrorCS"),sQuery(id+"F11.wireOp",EDGE,"E447.MirrorCS"),sQuery(id+"F11.wireOp",EDGE,"E448.MirrorCS"),sQuery(id+"F11.wireOp",EDGE,"E449.MirrorCS"),sQuery(id+"F11.wireOp",EDGE,"E450.MirrorCS"),sQuery(id+"F11.wireOp",EDGE,"E451.MirrorCS")])]});
            var Q25;
            Q25=makeQuery(id+"F14.boolean.opBoolean","SPLIT",BODY,{"disambiguationData":[OD(0.0)],"derivedFrom":makeQuery(id+"F3.opExtrude","SWEPT_BODY",BODY,{"disambiguationData":[OSD([sQuery(id+"F2.wireOp",EDGE,"E111"),sQuery(id+"F2.wireOp",EDGE,"E112"),sQuery(id+"F2.wireOp",EDGE,"E113"),sQuery(id+"F2.wireOp",EDGE,"E114"),sQuery(id+"F2.wireOp",EDGE,"E115.MirrorCS"),sQuery(id+"F2.wireOp",EDGE,"E116.MirrorCS"),sQuery(id+"F2.wireOp",EDGE,"E117.MirrorCS"),sQuery(id+"F2.wireOp",EDGE,"E118.MirrorCS"),sQuery(id+"F2.wireOp",EDGE,"E119.MirrorCS"),sQuery(id+"F2.wireOp",EDGE,"E120.MirrorCS"),sQuery(id+"F2.wireOp",EDGE,"E121.MirrorCS"),sQuery(id+"F2.wireOp",EDGE,"E122.MirrorCS"),sQuery(id+"F2.wireOp",EDGE,"E123.MirrorCS"),sQuery(id+"F2.wireOp",EDGE,"E124.MirrorCS"),sQuery(id+"F2.wireOp",EDGE,"E125.MirrorCS"),sQuery(id+"F2.wireOp",EDGE,"E126.MirrorCS")])]})});
            var Q26;
            Q26=makeQuery(id+"F14.boolean.opBoolean","SPLIT",BODY,{"disambiguationData":[OD(1.0)],"derivedFrom":makeQuery(id+"F3.opExtrude","SWEPT_BODY",BODY,{"disambiguationData":[OSD([sQuery(id+"F2.wireOp",EDGE,"E111"),sQuery(id+"F2.wireOp",EDGE,"E112"),sQuery(id+"F2.wireOp",EDGE,"E113"),sQuery(id+"F2.wireOp",EDGE,"E114"),sQuery(id+"F2.wireOp",EDGE,"E115.MirrorCS"),sQuery(id+"F2.wireOp",EDGE,"E116.MirrorCS"),sQuery(id+"F2.wireOp",EDGE,"E117.MirrorCS"),sQuery(id+"F2.wireOp",EDGE,"E118.MirrorCS"),sQuery(id+"F2.wireOp",EDGE,"E119.MirrorCS"),sQuery(id+"F2.wireOp",EDGE,"E120.MirrorCS"),sQuery(id+"F2.wireOp",EDGE,"E121.MirrorCS"),sQuery(id+"F2.wireOp",EDGE,"E122.MirrorCS"),sQuery(id+"F2.wireOp",EDGE,"E123.MirrorCS"),sQuery(id+"F2.wireOp",EDGE,"E124.MirrorCS"),sQuery(id+"F2.wireOp",EDGE,"E125.MirrorCS"),sQuery(id+"F2.wireOp",EDGE,"E126.MirrorCS")])]})});
            booleanBodies(context, id + "F15", {"operationType" : BooleanOperationType.UNION, "tools" : qUnion([Q0, Q1, Q2, Q3, Q4, Q5, Q6, Q7, Q8, Q9, Q10, Q11, Q12, Q13, Q14, Q15, Q16, Q17, Q18, Q19, Q20, Q21, Q22, Q23, Q24, Q25, Q26])});
        }
        {
            var Q0;
            Q0=makeQuery(id+"F5.opExtrude","SWEPT_FACE",FACE,{"disambiguationData":[OSD([sQuery(id+"F4.wireOp",EDGE,"E180.MirrorCS"),sQuery(id+"F4.wireOp",EDGE,"E185.MirrorCS")])]});
            var sketch = newSketch(context, id + "F16", { "sketchPlane" : qUnion([Q0])});
            skPoint(sketch, "E459.0", {"position": v(-4387.8, -92.68) * mm});
            skPoint(sketch, "E460.0", {"position": v(-2924.09, -61.76) * mm});
            skLineSegment(sketch, "E461", {"start": v(-4387.8, -92.68) * mm, "end": v(-2924.09, -61.76) * mm, "construction": true});
            skLineSegment(sketch, "E462", {"start": v(-3655.94, -77.22) * mm, "end": v(-3655.94, -2387.6) * mm, "construction": true});
            skCircle(sketch, "E463", {"center": v(-3655.94, -2387.6) * mm, "radius": 3.18 * mm});
            skSolve(sketch);
        }
        {
            var Q0;
            Q0 = qSketchRegion(id + "F16", true);
            extrude(context, id + "F17", {"entities" : qUnion([Q0]), "operationType" : NewBodyOperationType.REMOVE, "oppositeDirection" : true, "depth" : 216.71 * mm, "symmetric" : true});
        }
    });
